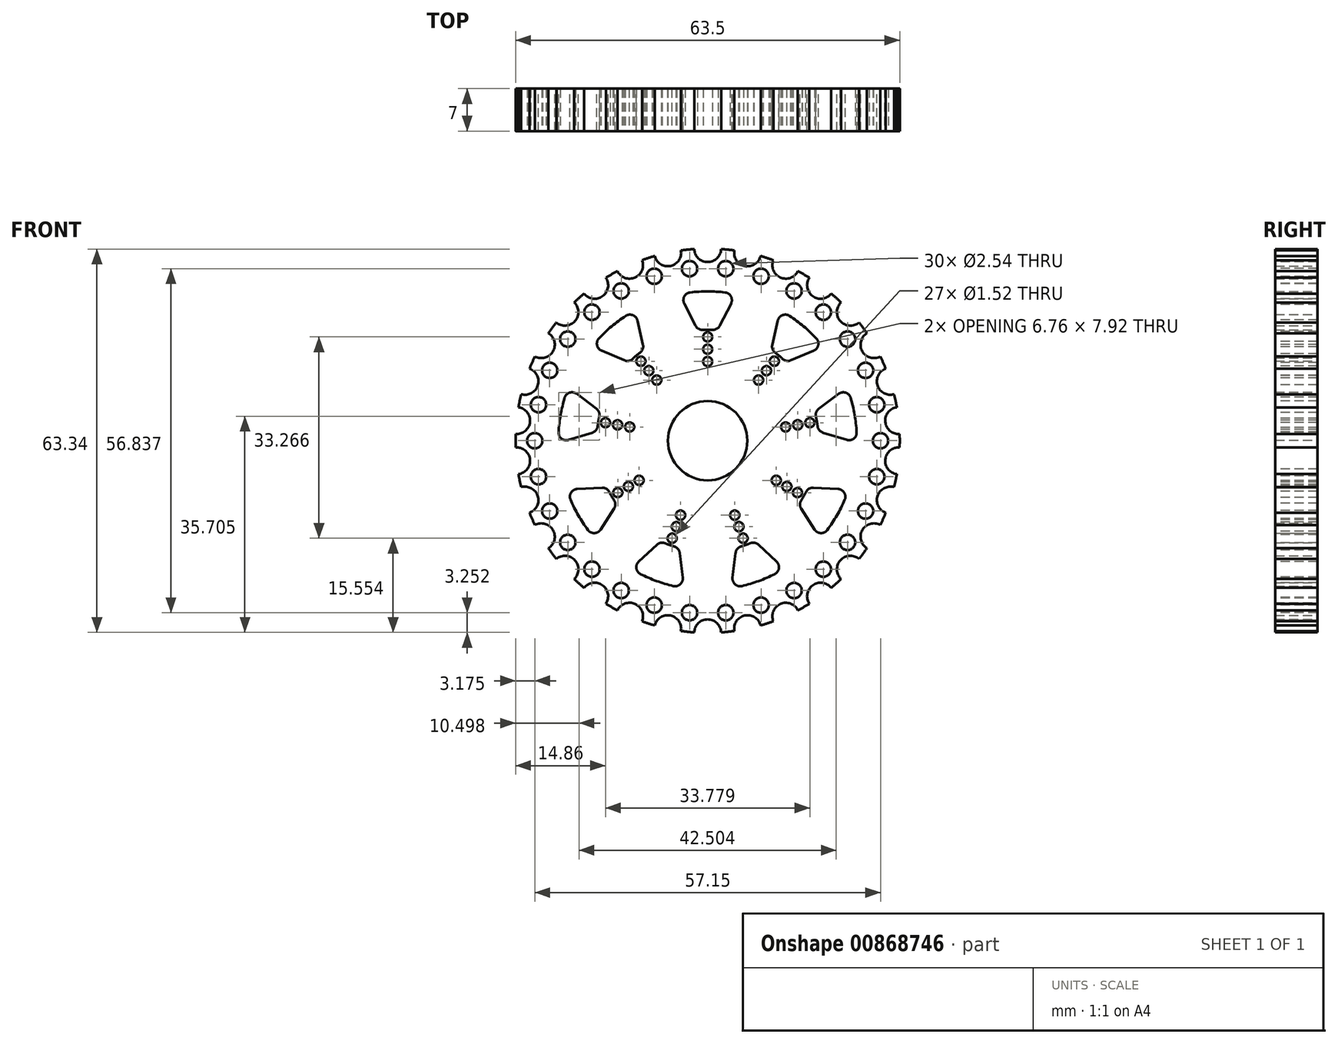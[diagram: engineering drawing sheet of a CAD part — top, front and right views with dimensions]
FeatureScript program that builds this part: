
annotation { "Feature Type Name" : "Feature", "Feature Type Description" : "" }
export const myFeature = defineFeature(function(context is Context, id is Id, definition is map)
    precondition{}
    {
        {
            var Q0;
            Q0=qCreatedBy(makeId("Front.planeOp"),FACE);
            var sketch = newSketch(context, id + "F0", { "sketchPlane" : qUnion([Q0])});
            skArc(sketch, "E0", {"start": v(-31.73, 1.1) * mm, "mid": v(-31.75, 0) * mm, "end": v(-31.73, -1.1) * mm});
            skPoint(sketch, "E1.end.orphan", {"position": v(-54.25, -98.6) * mm});
            skPoint(sketch, "E2.end.orphan", {"position": v(183.76, 0) * mm});
            skPoint(sketch, "E3.center.orphan", {"position": v(0, 98.6) * mm});
            skPoint(sketch, "E3.end.orphan", {"position": v(54.25, 98.6) * mm});
            skPoint(sketch, "E3.start.orphan", {"position": v(-54.25, 98.6) * mm});
            skCircle(sketch, "E4", {"center": v(0, 31.75) * mm, "radius": 2.22 * mm});
            skArc(sketch, "E5.9.0", {"start": v(-0.82, 33.81) * mm, "mid": v(-1.28, 29.93) * mm, "end": v(2.22, 31.67) * mm});
            skArc(sketch, "E5.10.0", {"start": v(-1.25, 33.59) * mm, "mid": v(-1.08, 29.8) * mm, "end": v(2.22, 31.67) * mm});
            skArc(sketch, "E5.13.0", {"start": v(-2.1, 32.46) * mm, "mid": v(-0.4, 29.56) * mm, "end": v(2.22, 31.67) * mm});
            skArc(sketch, "E5.18.0", {"start": v(-0.82, 33.81) * mm, "mid": v(-1.28, 29.93) * mm, "end": v(2.22, 31.67) * mm});
            skArc(sketch, "E5.19.0", {"start": v(-0.82, 33.81) * mm, "mid": v(-1.28, 29.93) * mm, "end": v(2.22, 31.67) * mm});
            skLineSegment(sketch, "E5.anchor1", {"start": v(0, 0) * mm, "end": v(0, 31.75) * mm, "construction": true});
            skLineSegment(sketch, "E5.anchor2", {"start": v(0, 0) * mm, "end": v(0, 31.75) * mm, "construction": true});
            skPoint(sketch, "E6.center", {"position": v(-2.61, -0.33) * mm});
            skArc(sketch, "E7.1.0", {"start": v(-8.76, 30.52) * mm, "mid": v(-6.14, 28.88) * mm, "end": v(-4.41, 31.44) * mm});
            skArc(sketch, "E7.2.0", {"start": v(-14.91, 28.03) * mm, "mid": v(-12, 26.97) * mm, "end": v(-10.85, 29.84) * mm});
            skArc(sketch, "E7.3.0", {"start": v(-20.41, 24.32) * mm, "mid": v(-17.36, 23.89) * mm, "end": v(-16.82, 26.93) * mm});
            skArc(sketch, "E7.4.0", {"start": v(-25.02, 19.54) * mm, "mid": v(-21.94, 19.76) * mm, "end": v(-22.05, 22.84) * mm});
            skArc(sketch, "E7.5.0", {"start": v(-28.54, 13.91) * mm, "mid": v(-25.57, 14.76) * mm, "end": v(-26.32, 17.76) * mm});
            skArc(sketch, "E7.6.0", {"start": v(-30.8, 7.67) * mm, "mid": v(-28.08, 9.12) * mm, "end": v(-29.44, 11.9) * mm});
            skArc(sketch, "E7.7.0", {"start": v(-31.73, 1.1) * mm, "mid": v(-29.37, 3.09) * mm, "end": v(-31.27, 5.52) * mm});
            skArc(sketch, "E7.8.0", {"start": v(-31.27, -5.52) * mm, "mid": v(-29.37, -3.09) * mm, "end": v(-31.73, -1.1) * mm});
            skArc(sketch, "E7.9.0", {"start": v(-29.44, -11.9) * mm, "mid": v(-28.08, -9.12) * mm, "end": v(-30.8, -7.67) * mm});
            skArc(sketch, "E7.10.0", {"start": v(-26.32, -17.76) * mm, "mid": v(-25.57, -14.76) * mm, "end": v(-28.54, -13.91) * mm});
            skArc(sketch, "E7.11.0", {"start": v(-22.05, -22.84) * mm, "mid": v(-21.94, -19.76) * mm, "end": v(-25.02, -19.54) * mm});
            skArc(sketch, "E7.12.0", {"start": v(-16.82, -26.93) * mm, "mid": v(-17.36, -23.89) * mm, "end": v(-20.41, -24.32) * mm});
            skArc(sketch, "E7.13.0", {"start": v(-10.85, -29.84) * mm, "mid": v(-12, -26.97) * mm, "end": v(-14.91, -28.03) * mm});
            skArc(sketch, "E7.14.0", {"start": v(-4.41, -31.44) * mm, "mid": v(-6.14, -28.88) * mm, "end": v(-8.76, -30.52) * mm});
            skArc(sketch, "E7.15.0", {"start": v(2.22, -31.67) * mm, "mid": v(0, -29.53) * mm, "end": v(-2.22, -31.67) * mm});
            skArc(sketch, "E7.16.0", {"start": v(8.76, -30.52) * mm, "mid": v(6.14, -28.88) * mm, "end": v(4.41, -31.44) * mm});
            skArc(sketch, "E7.17.0", {"start": v(14.91, -28.03) * mm, "mid": v(12, -26.97) * mm, "end": v(10.85, -29.84) * mm});
            skArc(sketch, "E7.18.0", {"start": v(20.41, -24.32) * mm, "mid": v(17.36, -23.89) * mm, "end": v(16.82, -26.93) * mm});
            skArc(sketch, "E7.19.0", {"start": v(25.02, -19.54) * mm, "mid": v(21.94, -19.76) * mm, "end": v(22.05, -22.84) * mm});
            skArc(sketch, "E7.20.0", {"start": v(28.54, -13.91) * mm, "mid": v(25.57, -14.76) * mm, "end": v(26.32, -17.76) * mm});
            skArc(sketch, "E7.21.0", {"start": v(30.8, -7.67) * mm, "mid": v(28.08, -9.12) * mm, "end": v(29.44, -11.9) * mm});
            skArc(sketch, "E7.22.0", {"start": v(31.73, -1.1) * mm, "mid": v(29.37, -3.09) * mm, "end": v(31.27, -5.52) * mm});
            skArc(sketch, "E7.23.0", {"start": v(31.27, 5.52) * mm, "mid": v(29.37, 3.09) * mm, "end": v(31.73, 1.1) * mm});
            skArc(sketch, "E7.24.0", {"start": v(29.44, 11.9) * mm, "mid": v(28.08, 9.12) * mm, "end": v(30.8, 7.67) * mm});
            skArc(sketch, "E7.25.0", {"start": v(26.32, 17.76) * mm, "mid": v(25.57, 14.76) * mm, "end": v(28.54, 13.91) * mm});
            skArc(sketch, "E7.26.0", {"start": v(22.05, 22.84) * mm, "mid": v(21.94, 19.76) * mm, "end": v(25.02, 19.54) * mm});
            skArc(sketch, "E7.27.0", {"start": v(16.82, 26.93) * mm, "mid": v(17.36, 23.89) * mm, "end": v(20.41, 24.32) * mm});
            skArc(sketch, "E7.28.0", {"start": v(10.85, 29.84) * mm, "mid": v(12, 26.97) * mm, "end": v(14.91, 28.03) * mm});
            skArc(sketch, "E7.29.0", {"start": v(4.41, 31.44) * mm, "mid": v(6.14, 28.88) * mm, "end": v(8.76, 30.52) * mm});
            skArc(sketch, "E8.trimOffspring", {"start": v(-30.8, 7.67) * mm, "mid": v(-31.06, 6.6) * mm, "end": v(-31.27, 5.52) * mm});
            skArc(sketch, "E9.trimOffspring", {"start": v(-28.54, 13.91) * mm, "mid": v(-29, 12.91) * mm, "end": v(-29.44, 11.9) * mm});
            skArc(sketch, "E10.trimOffspring", {"start": v(-25.02, 19.54) * mm, "mid": v(-25.69, 18.66) * mm, "end": v(-26.32, 17.76) * mm});
            skArc(sketch, "E11.trimOffspring", {"start": v(-20.41, 24.32) * mm, "mid": v(-21.24, 23.6) * mm, "end": v(-22.05, 22.84) * mm});
            skArc(sketch, "E12.trimOffspring", {"start": v(-14.91, 28.03) * mm, "mid": v(-15.88, 27.5) * mm, "end": v(-16.82, 26.93) * mm});
            skArc(sketch, "E13.trimOffspring", {"start": v(-8.76, 30.52) * mm, "mid": v(-9.81, 30.2) * mm, "end": v(-10.85, 29.84) * mm});
            skArc(sketch, "E14.trimOffspring", {"start": v(-2.22, 31.67) * mm, "mid": v(-3.32, 31.58) * mm, "end": v(-4.41, 31.44) * mm});
            skArc(sketch, "E15.trimOffspring", {"start": v(4.41, 31.44) * mm, "mid": v(3.32, 31.58) * mm, "end": v(2.22, 31.67) * mm});
            skArc(sketch, "E16.trimOffspring", {"start": v(10.85, 29.84) * mm, "mid": v(9.81, 30.2) * mm, "end": v(8.76, 30.52) * mm});
            skArc(sketch, "E17.trimOffspring", {"start": v(16.82, 26.93) * mm, "mid": v(15.88, 27.5) * mm, "end": v(14.91, 28.03) * mm});
            skArc(sketch, "E18.trimOffspring", {"start": v(22.05, 22.84) * mm, "mid": v(21.24, 23.6) * mm, "end": v(20.41, 24.32) * mm});
            skArc(sketch, "E19.trimOffspring", {"start": v(26.32, 17.76) * mm, "mid": v(25.69, 18.66) * mm, "end": v(25.02, 19.54) * mm});
            skArc(sketch, "E20.trimOffspring", {"start": v(29.44, 11.9) * mm, "mid": v(29, 12.91) * mm, "end": v(28.54, 13.91) * mm});
            skArc(sketch, "E21.trimOffspring", {"start": v(31.27, 5.52) * mm, "mid": v(31.06, 6.6) * mm, "end": v(30.8, 7.67) * mm});
            skArc(sketch, "E22.trimOffspring", {"start": v(31.73, -1.1) * mm, "mid": v(31.75, 0) * mm, "end": v(31.73, 1.1) * mm});
            skArc(sketch, "E23.trimOffspring", {"start": v(30.8, -7.67) * mm, "mid": v(31.06, -6.6) * mm, "end": v(31.27, -5.52) * mm});
            skArc(sketch, "E24.trimOffspring", {"start": v(28.54, -13.91) * mm, "mid": v(29, -12.91) * mm, "end": v(29.44, -11.9) * mm});
            skArc(sketch, "E25.trimOffspring", {"start": v(25.02, -19.54) * mm, "mid": v(25.69, -18.66) * mm, "end": v(26.32, -17.76) * mm});
            skArc(sketch, "E26.trimOffspring", {"start": v(20.41, -24.32) * mm, "mid": v(21.24, -23.6) * mm, "end": v(22.05, -22.84) * mm});
            skArc(sketch, "E27.trimOffspring", {"start": v(14.91, -28.03) * mm, "mid": v(15.87, -27.5) * mm, "end": v(16.82, -26.93) * mm});
            skArc(sketch, "E28.trimOffspring", {"start": v(-31.27, -5.52) * mm, "mid": v(-31.06, -6.6) * mm, "end": v(-30.8, -7.67) * mm});
            skArc(sketch, "E29.trimOffspring", {"start": v(-29.44, -11.9) * mm, "mid": v(-29, -12.91) * mm, "end": v(-28.54, -13.91) * mm});
            skArc(sketch, "E30.trimOffspring", {"start": v(-26.32, -17.76) * mm, "mid": v(-25.69, -18.66) * mm, "end": v(-25.02, -19.54) * mm});
            skArc(sketch, "E31.trimOffspring", {"start": v(-22.05, -22.84) * mm, "mid": v(-21.24, -23.6) * mm, "end": v(-20.41, -24.32) * mm});
            skArc(sketch, "E32.trimOffspring", {"start": v(-16.82, -26.93) * mm, "mid": v(-15.87, -27.5) * mm, "end": v(-14.91, -28.03) * mm});
            skArc(sketch, "E33.trimOffspring", {"start": v(-10.85, -29.84) * mm, "mid": v(-9.81, -30.2) * mm, "end": v(-8.76, -30.52) * mm});
            skArc(sketch, "E34.trimOffspring", {"start": v(-4.41, -31.44) * mm, "mid": v(-3.32, -31.58) * mm, "end": v(-2.22, -31.67) * mm});
            skArc(sketch, "E35.trimOffspring", {"start": v(2.22, -31.67) * mm, "mid": v(3.32, -31.58) * mm, "end": v(4.41, -31.44) * mm});
            skArc(sketch, "E36.trimOffspring", {"start": v(8.76, -30.52) * mm, "mid": v(9.81, -30.2) * mm, "end": v(10.85, -29.84) * mm});
            skCircle(sketch, "E37", {"center": v(0, 0) * mm, "radius": 6.35 * mm, "construction": true});
            skLineSegment(sketch, "E38", {"start": v(-3.87, 22.66) * mm, "end": v(-2, 19.01) * mm});
            skArc(sketch, "E39", {"start": v(-0.82, 18.32) * mm, "mid": v(-0.4, 18.33) * mm, "end": v(0, 18.34) * mm});
            skArc(sketch, "E40", {"start": v(-2.89, 24.5) * mm, "mid": v(-1.45, 24.63) * mm, "end": v(0, 24.67) * mm});
            skPoint(sketch, "E41.visualSharp", {"position": v(-4.67, 24.23) * mm});
            skArc(sketch, "E41.filletArc", {"start": v(-2.89, 24.5) * mm, "mid": v(-3.86, 23.84) * mm, "end": v(-3.87, 22.66) * mm});
            skPoint(sketch, "E42.visualSharp", {"position": v(-1.62, 18.27) * mm});
            skArc(sketch, "E42.filletArc", {"start": v(-2, 19.01) * mm, "mid": v(-1.51, 18.5) * mm, "end": v(-0.82, 18.32) * mm});
            skPoint(sketch, "E43.start.orphan", {"position": v(4.67, 24.23) * mm});
            skPoint(sketch, "E44.orphan", {"position": v(1.62, 18.27) * mm});
            skArc(sketch, "E45.MirrorCS", {"start": v(2.89, 24.5) * mm, "mid": v(1.45, 24.63) * mm, "end": v(0, 24.67) * mm});
            skArc(sketch, "E46.MirrorCS", {"start": v(2.89, 24.5) * mm, "mid": v(3.86, 23.84) * mm, "end": v(3.87, 22.66) * mm});
            skLineSegment(sketch, "E47.MirrorCS", {"start": v(3.87, 22.66) * mm, "end": v(2, 19.01) * mm});
            skArc(sketch, "E48.MirrorCS", {"start": v(2, 19.01) * mm, "mid": v(1.51, 18.5) * mm, "end": v(0.82, 18.32) * mm});
            skArc(sketch, "E49.MirrorCS", {"start": v(0.82, 18.32) * mm, "mid": v(0.4, 18.33) * mm, "end": v(0, 18.34) * mm});
            skLineSegment(sketch, "E50.anchor1", {"start": v(0, 0) * mm, "end": v(-1.62, 18.27) * mm, "construction": true});
            skLineSegment(sketch, "E50.anchor2", {"start": v(0, 0) * mm, "end": v(-1.62, 18.27) * mm, "construction": true});
            skPoint(sketch, "E51.1.0", {"position": v(-12, 21.56) * mm});
            skPoint(sketch, "E51.1.1", {"position": v(-19.15, 15.56) * mm});
            skLineSegment(sketch, "E51.1.2", {"start": v(-17.53, 14.88) * mm, "end": v(-13.75, 13.28) * mm});
            skLineSegment(sketch, "E51.1.3", {"start": v(-11.6, 19.85) * mm, "end": v(-10.69, 15.85) * mm});
            skArc(sketch, "E51.1.4", {"start": v(-13.54, 20.63) * mm, "mid": v(-14.73, 19.8) * mm, "end": v(-15.86, 18.9) * mm});
            skArc(sketch, "E51.1.5", {"start": v(-13.54, 20.63) * mm, "mid": v(-12.37, 20.74) * mm, "end": v(-11.6, 19.85) * mm});
            skArc(sketch, "E51.1.6", {"start": v(-17.96, 16.92) * mm, "mid": v(-16.94, 17.94) * mm, "end": v(-15.86, 18.9) * mm});
            skArc(sketch, "E51.1.7", {"start": v(-17.96, 16.92) * mm, "mid": v(-18.28, 15.78) * mm, "end": v(-17.53, 14.88) * mm});
            skLineSegment(sketch, "E51.1.8", {"start": v(-17.53, 14.88) * mm, "end": v(-13.75, 13.28) * mm});
            skArc(sketch, "E51.1.9", {"start": v(-13.54, 20.63) * mm, "mid": v(-14.73, 19.8) * mm, "end": v(-15.86, 18.9) * mm});
            skArc(sketch, "E51.1.10", {"start": v(-17.96, 16.92) * mm, "mid": v(-18.28, 15.78) * mm, "end": v(-17.53, 14.88) * mm});
            skPoint(sketch, "E51.1.11", {"position": v(-12, 21.56) * mm});
            skLineSegment(sketch, "E51.1.12", {"start": v(-11.6, 19.85) * mm, "end": v(-10.69, 15.85) * mm});
            skArc(sketch, "E51.1.13", {"start": v(-17.96, 16.92) * mm, "mid": v(-16.94, 17.94) * mm, "end": v(-15.86, 18.9) * mm});
            skPoint(sketch, "E51.1.14", {"position": v(-19.15, 15.56) * mm});
            skPoint(sketch, "E51.1.15", {"position": v(-10.5, 15.04) * mm});
            skPoint(sketch, "E51.1.16", {"position": v(-12.98, 12.95) * mm});
            skArc(sketch, "E51.1.17", {"start": v(-13.54, 20.63) * mm, "mid": v(-12.37, 20.74) * mm, "end": v(-11.6, 19.85) * mm});
            skArc(sketch, "E51.1.18", {"start": v(-17.96, 16.92) * mm, "mid": v(-18.28, 15.78) * mm, "end": v(-17.53, 14.88) * mm});
            skLineSegment(sketch, "E51.1.19", {"start": v(-17.53, 14.88) * mm, "end": v(-13.75, 13.28) * mm});
            skPoint(sketch, "E51.1.20", {"position": v(-12, 21.56) * mm});
            skArc(sketch, "E51.1.21", {"start": v(-13.54, 20.63) * mm, "mid": v(-14.73, 19.8) * mm, "end": v(-15.86, 18.9) * mm});
            skPoint(sketch, "E51.1.22", {"position": v(-10.5, 15.04) * mm});
            skArc(sketch, "E51.1.23", {"start": v(-17.96, 16.92) * mm, "mid": v(-16.94, 17.94) * mm, "end": v(-15.86, 18.9) * mm});
            skPoint(sketch, "E51.1.24", {"position": v(-12.98, 12.95) * mm});
            skPoint(sketch, "E51.1.25", {"position": v(-19.15, 15.56) * mm});
            skLineSegment(sketch, "E51.1.26", {"start": v(-11.6, 19.85) * mm, "end": v(-10.69, 15.85) * mm});
            skArc(sketch, "E51.1.27", {"start": v(-13.54, 20.63) * mm, "mid": v(-12.37, 20.74) * mm, "end": v(-11.6, 19.85) * mm});
            skLineSegment(sketch, "E51.1.28", {"start": v(-17.53, 14.88) * mm, "end": v(-13.75, 13.28) * mm});
            skPoint(sketch, "E51.1.29", {"position": v(-12.98, 12.95) * mm});
            skArc(sketch, "E51.1.30", {"start": v(-17.96, 16.92) * mm, "mid": v(-16.94, 17.94) * mm, "end": v(-15.86, 18.9) * mm});
            skPoint(sketch, "E51.1.31", {"position": v(-19.15, 15.56) * mm});
            skPoint(sketch, "E51.1.32", {"position": v(-12, 21.56) * mm});
            skLineSegment(sketch, "E51.1.33", {"start": v(-11.6, 19.85) * mm, "end": v(-10.69, 15.85) * mm});
            skArc(sketch, "E51.1.34", {"start": v(-13.54, 20.63) * mm, "mid": v(-14.73, 19.8) * mm, "end": v(-15.86, 18.9) * mm});
            skArc(sketch, "E51.1.35", {"start": v(-17.96, 16.92) * mm, "mid": v(-18.28, 15.78) * mm, "end": v(-17.53, 14.88) * mm});
            skArc(sketch, "E51.1.36", {"start": v(-13.54, 20.63) * mm, "mid": v(-12.37, 20.74) * mm, "end": v(-11.6, 19.85) * mm});
            skPoint(sketch, "E51.1.37", {"position": v(-10.5, 15.04) * mm});
            skArc(sketch, "E51.1.38", {"start": v(-13.54, 20.63) * mm, "mid": v(-14.73, 19.8) * mm, "end": v(-15.86, 18.9) * mm});
            skArc(sketch, "E51.1.39", {"start": v(-17.96, 16.92) * mm, "mid": v(-16.94, 17.94) * mm, "end": v(-15.86, 18.9) * mm});
            skLineSegment(sketch, "E51.1.40", {"start": v(-11.6, 19.85) * mm, "end": v(-10.69, 15.85) * mm});
            skPoint(sketch, "E51.1.41", {"position": v(-12, 21.56) * mm});
            skArc(sketch, "E51.1.42", {"start": v(-17.96, 16.92) * mm, "mid": v(-18.28, 15.78) * mm, "end": v(-17.53, 14.88) * mm});
            skPoint(sketch, "E51.1.43", {"position": v(-10.5, 15.04) * mm});
            skPoint(sketch, "E51.1.44", {"position": v(-19.15, 15.56) * mm});
            skPoint(sketch, "E51.1.45", {"position": v(-12.98, 12.95) * mm});
            skLineSegment(sketch, "E51.1.46", {"start": v(-17.53, 14.88) * mm, "end": v(-13.75, 13.28) * mm});
            skArc(sketch, "E51.1.47", {"start": v(-13.54, 20.63) * mm, "mid": v(-12.37, 20.74) * mm, "end": v(-11.6, 19.85) * mm});
            skPoint(sketch, "E51.1.48", {"position": v(-10.5, 15.04) * mm});
            skPoint(sketch, "E51.1.49", {"position": v(-12.98, 12.95) * mm});
            skArc(sketch, "E51.1.50", {"start": v(-10.69, 15.85) * mm, "mid": v(-10.73, 15.14) * mm, "end": v(-11.15, 14.56) * mm});
            skArc(sketch, "E51.1.51", {"start": v(-10.69, 15.85) * mm, "mid": v(-10.73, 15.14) * mm, "end": v(-11.15, 14.56) * mm});
            skArc(sketch, "E51.1.52", {"start": v(-13.75, 13.28) * mm, "mid": v(-13.04, 13.2) * mm, "end": v(-12.4, 13.5) * mm});
            skArc(sketch, "E51.1.53", {"start": v(-10.69, 15.85) * mm, "mid": v(-10.73, 15.14) * mm, "end": v(-11.15, 14.56) * mm});
            skArc(sketch, "E51.1.54", {"start": v(-10.69, 15.85) * mm, "mid": v(-10.73, 15.14) * mm, "end": v(-11.15, 14.56) * mm});
            skArc(sketch, "E51.1.55", {"start": v(-13.75, 13.28) * mm, "mid": v(-13.04, 13.2) * mm, "end": v(-12.4, 13.5) * mm});
            skArc(sketch, "E51.1.56", {"start": v(-10.69, 15.85) * mm, "mid": v(-10.73, 15.14) * mm, "end": v(-11.15, 14.56) * mm});
            skArc(sketch, "E51.1.57", {"start": v(-13.75, 13.28) * mm, "mid": v(-13.04, 13.2) * mm, "end": v(-12.4, 13.5) * mm});
            skArc(sketch, "E51.1.58", {"start": v(-11.15, 14.56) * mm, "mid": v(-11.47, 14.3) * mm, "end": v(-11.79, 14.05) * mm});
            skArc(sketch, "E51.1.59", {"start": v(-13.75, 13.28) * mm, "mid": v(-13.04, 13.2) * mm, "end": v(-12.4, 13.5) * mm});
            skArc(sketch, "E51.1.60", {"start": v(-12.4, 13.5) * mm, "mid": v(-12.1, 13.78) * mm, "end": v(-11.79, 14.05) * mm});
            skArc(sketch, "E51.1.61", {"start": v(-12.4, 13.5) * mm, "mid": v(-12.1, 13.78) * mm, "end": v(-11.79, 14.05) * mm});
            skArc(sketch, "E51.1.62", {"start": v(-13.75, 13.28) * mm, "mid": v(-13.04, 13.2) * mm, "end": v(-12.4, 13.5) * mm});
            skArc(sketch, "E51.1.63", {"start": v(-11.15, 14.56) * mm, "mid": v(-11.47, 14.3) * mm, "end": v(-11.79, 14.05) * mm});
            skArc(sketch, "E51.1.64", {"start": v(-12.4, 13.5) * mm, "mid": v(-12.1, 13.78) * mm, "end": v(-11.79, 14.05) * mm});
            skArc(sketch, "E51.1.65", {"start": v(-11.15, 14.56) * mm, "mid": v(-11.47, 14.3) * mm, "end": v(-11.79, 14.05) * mm});
            skArc(sketch, "E51.1.66", {"start": v(-11.15, 14.56) * mm, "mid": v(-11.47, 14.3) * mm, "end": v(-11.79, 14.05) * mm});
            skArc(sketch, "E51.1.67", {"start": v(-12.4, 13.5) * mm, "mid": v(-12.1, 13.78) * mm, "end": v(-11.79, 14.05) * mm});
            skArc(sketch, "E51.1.68", {"start": v(-12.4, 13.5) * mm, "mid": v(-12.1, 13.78) * mm, "end": v(-11.79, 14.05) * mm});
            skArc(sketch, "E51.1.69", {"start": v(-11.15, 14.56) * mm, "mid": v(-11.47, 14.3) * mm, "end": v(-11.79, 14.05) * mm});
            skPoint(sketch, "E51.2.0", {"position": v(-23.05, 8.8) * mm});
            skPoint(sketch, "E51.2.1", {"position": v(-24.67, -0.39) * mm});
            skLineSegment(sketch, "E51.2.2", {"start": v(-23, 0.13) * mm, "end": v(-19.07, 1.33) * mm});
            skLineSegment(sketch, "E51.2.3", {"start": v(-21.65, 7.74) * mm, "end": v(-18.37, 5.27) * mm});
            skArc(sketch, "E51.2.4", {"start": v(-23.63, 7.1) * mm, "mid": v(-24, 5.7) * mm, "end": v(-24.3, 4.28) * mm});
            skArc(sketch, "E51.2.5", {"start": v(-23.63, 7.1) * mm, "mid": v(-22.8, 7.94) * mm, "end": v(-21.65, 7.74) * mm});
            skArc(sketch, "E51.2.6", {"start": v(-24.63, 1.41) * mm, "mid": v(-24.5, 2.85) * mm, "end": v(-24.3, 4.28) * mm});
            skArc(sketch, "E51.2.7", {"start": v(-24.63, 1.41) * mm, "mid": v(-24.15, 0.34) * mm, "end": v(-23, 0.13) * mm});
            skLineSegment(sketch, "E51.2.8", {"start": v(-23, 0.13) * mm, "end": v(-19.07, 1.33) * mm});
            skArc(sketch, "E51.2.9", {"start": v(-23.63, 7.1) * mm, "mid": v(-24, 5.7) * mm, "end": v(-24.3, 4.28) * mm});
            skArc(sketch, "E51.2.10", {"start": v(-24.63, 1.41) * mm, "mid": v(-24.15, 0.34) * mm, "end": v(-23, 0.13) * mm});
            skPoint(sketch, "E51.2.11", {"position": v(-23.05, 8.8) * mm});
            skLineSegment(sketch, "E51.2.12", {"start": v(-21.65, 7.74) * mm, "end": v(-18.37, 5.27) * mm});
            skArc(sketch, "E51.2.13", {"start": v(-24.63, 1.41) * mm, "mid": v(-24.5, 2.85) * mm, "end": v(-24.3, 4.28) * mm});
            skPoint(sketch, "E51.2.14", {"position": v(-24.67, -0.39) * mm});
            skPoint(sketch, "E51.2.15", {"position": v(-17.7, 4.77) * mm});
            skPoint(sketch, "E51.2.16", {"position": v(-18.27, 1.57) * mm});
            skArc(sketch, "E51.2.17", {"start": v(-23.63, 7.1) * mm, "mid": v(-22.8, 7.94) * mm, "end": v(-21.65, 7.74) * mm});
            skArc(sketch, "E51.2.18", {"start": v(-24.63, 1.41) * mm, "mid": v(-24.15, 0.34) * mm, "end": v(-23, 0.13) * mm});
            skLineSegment(sketch, "E51.2.19", {"start": v(-23, 0.13) * mm, "end": v(-19.07, 1.33) * mm});
            skPoint(sketch, "E51.2.20", {"position": v(-23.05, 8.8) * mm});
            skArc(sketch, "E51.2.21", {"start": v(-23.63, 7.1) * mm, "mid": v(-24, 5.7) * mm, "end": v(-24.3, 4.28) * mm});
            skPoint(sketch, "E51.2.22", {"position": v(-17.7, 4.77) * mm});
            skArc(sketch, "E51.2.23", {"start": v(-24.63, 1.41) * mm, "mid": v(-24.5, 2.85) * mm, "end": v(-24.3, 4.28) * mm});
            skPoint(sketch, "E51.2.24", {"position": v(-18.27, 1.57) * mm});
            skPoint(sketch, "E51.2.25", {"position": v(-24.67, -0.39) * mm});
            skLineSegment(sketch, "E51.2.26", {"start": v(-21.65, 7.74) * mm, "end": v(-18.37, 5.27) * mm});
            skArc(sketch, "E51.2.27", {"start": v(-23.63, 7.1) * mm, "mid": v(-22.8, 7.94) * mm, "end": v(-21.65, 7.74) * mm});
            skLineSegment(sketch, "E51.2.28", {"start": v(-23, 0.13) * mm, "end": v(-19.07, 1.33) * mm});
            skPoint(sketch, "E51.2.29", {"position": v(-18.27, 1.57) * mm});
            skArc(sketch, "E51.2.30", {"start": v(-24.63, 1.41) * mm, "mid": v(-24.5, 2.85) * mm, "end": v(-24.3, 4.28) * mm});
            skPoint(sketch, "E51.2.31", {"position": v(-24.67, -0.39) * mm});
            skPoint(sketch, "E51.2.32", {"position": v(-23.05, 8.8) * mm});
            skLineSegment(sketch, "E51.2.33", {"start": v(-21.65, 7.74) * mm, "end": v(-18.37, 5.27) * mm});
            skArc(sketch, "E51.2.34", {"start": v(-23.63, 7.1) * mm, "mid": v(-24, 5.7) * mm, "end": v(-24.3, 4.28) * mm});
            skArc(sketch, "E51.2.35", {"start": v(-24.63, 1.41) * mm, "mid": v(-24.15, 0.34) * mm, "end": v(-23, 0.13) * mm});
            skArc(sketch, "E51.2.36", {"start": v(-23.63, 7.1) * mm, "mid": v(-22.8, 7.94) * mm, "end": v(-21.65, 7.74) * mm});
            skPoint(sketch, "E51.2.37", {"position": v(-17.7, 4.77) * mm});
            skArc(sketch, "E51.2.38", {"start": v(-23.63, 7.1) * mm, "mid": v(-24, 5.7) * mm, "end": v(-24.3, 4.28) * mm});
            skArc(sketch, "E51.2.39", {"start": v(-24.63, 1.41) * mm, "mid": v(-24.5, 2.85) * mm, "end": v(-24.3, 4.28) * mm});
            skLineSegment(sketch, "E51.2.40", {"start": v(-21.65, 7.74) * mm, "end": v(-18.37, 5.27) * mm});
            skPoint(sketch, "E51.2.41", {"position": v(-23.05, 8.8) * mm});
            skArc(sketch, "E51.2.42", {"start": v(-24.63, 1.41) * mm, "mid": v(-24.15, 0.34) * mm, "end": v(-23, 0.13) * mm});
            skPoint(sketch, "E51.2.43", {"position": v(-17.7, 4.77) * mm});
            skPoint(sketch, "E51.2.44", {"position": v(-24.67, -0.39) * mm});
            skPoint(sketch, "E51.2.45", {"position": v(-18.27, 1.57) * mm});
            skLineSegment(sketch, "E51.2.46", {"start": v(-23, 0.13) * mm, "end": v(-19.07, 1.33) * mm});
            skArc(sketch, "E51.2.47", {"start": v(-23.63, 7.1) * mm, "mid": v(-22.8, 7.94) * mm, "end": v(-21.65, 7.74) * mm});
            skPoint(sketch, "E51.2.48", {"position": v(-17.7, 4.77) * mm});
            skPoint(sketch, "E51.2.49", {"position": v(-18.27, 1.57) * mm});
            skArc(sketch, "E51.2.50", {"start": v(-18.37, 5.27) * mm, "mid": v(-17.95, 4.7) * mm, "end": v(-17.9, 3.98) * mm});
            skArc(sketch, "E51.2.51", {"start": v(-18.37, 5.27) * mm, "mid": v(-17.95, 4.7) * mm, "end": v(-17.9, 3.98) * mm});
            skArc(sketch, "E51.2.52", {"start": v(-19.07, 1.33) * mm, "mid": v(-18.47, 1.72) * mm, "end": v(-18.18, 2.38) * mm});
            skArc(sketch, "E51.2.53", {"start": v(-18.37, 5.27) * mm, "mid": v(-17.95, 4.7) * mm, "end": v(-17.9, 3.98) * mm});
            skArc(sketch, "E51.2.54", {"start": v(-18.37, 5.27) * mm, "mid": v(-17.95, 4.7) * mm, "end": v(-17.9, 3.98) * mm});
            skArc(sketch, "E51.2.55", {"start": v(-19.07, 1.33) * mm, "mid": v(-18.47, 1.72) * mm, "end": v(-18.18, 2.38) * mm});
            skArc(sketch, "E51.2.56", {"start": v(-18.37, 5.27) * mm, "mid": v(-17.95, 4.7) * mm, "end": v(-17.9, 3.98) * mm});
            skArc(sketch, "E51.2.57", {"start": v(-19.07, 1.33) * mm, "mid": v(-18.47, 1.72) * mm, "end": v(-18.18, 2.38) * mm});
            skArc(sketch, "E51.2.58", {"start": v(-17.9, 3.98) * mm, "mid": v(-17.98, 3.59) * mm, "end": v(-18.06, 3.18) * mm});
            skArc(sketch, "E51.2.59", {"start": v(-19.07, 1.33) * mm, "mid": v(-18.47, 1.72) * mm, "end": v(-18.18, 2.38) * mm});
            skArc(sketch, "E51.2.60", {"start": v(-18.18, 2.38) * mm, "mid": v(-18.12, 2.78) * mm, "end": v(-18.06, 3.18) * mm});
            skArc(sketch, "E51.2.61", {"start": v(-18.18, 2.38) * mm, "mid": v(-18.12, 2.78) * mm, "end": v(-18.06, 3.18) * mm});
            skArc(sketch, "E51.2.62", {"start": v(-19.07, 1.33) * mm, "mid": v(-18.47, 1.72) * mm, "end": v(-18.18, 2.38) * mm});
            skArc(sketch, "E51.2.63", {"start": v(-17.9, 3.98) * mm, "mid": v(-17.98, 3.59) * mm, "end": v(-18.06, 3.18) * mm});
            skArc(sketch, "E51.2.64", {"start": v(-18.18, 2.38) * mm, "mid": v(-18.12, 2.78) * mm, "end": v(-18.06, 3.18) * mm});
            skArc(sketch, "E51.2.65", {"start": v(-17.9, 3.98) * mm, "mid": v(-17.98, 3.59) * mm, "end": v(-18.06, 3.18) * mm});
            skArc(sketch, "E51.2.66", {"start": v(-17.9, 3.98) * mm, "mid": v(-17.98, 3.59) * mm, "end": v(-18.06, 3.18) * mm});
            skArc(sketch, "E51.2.67", {"start": v(-18.18, 2.38) * mm, "mid": v(-18.12, 2.78) * mm, "end": v(-18.06, 3.18) * mm});
            skArc(sketch, "E51.2.68", {"start": v(-18.18, 2.38) * mm, "mid": v(-18.12, 2.78) * mm, "end": v(-18.06, 3.18) * mm});
            skArc(sketch, "E51.2.69", {"start": v(-17.9, 3.98) * mm, "mid": v(-17.98, 3.59) * mm, "end": v(-18.06, 3.18) * mm});
            skPoint(sketch, "E52.0.3.0", {"position": v(-15, -10.54) * mm});
            skPoint(sketch, "E52.1.3.0", {"position": v(-18.65, -16.15) * mm});
            skLineSegment(sketch, "E52.2.3.0", {"start": v(-17.7, -14.68) * mm, "end": v(-15.46, -11.24) * mm});
            skLineSegment(sketch, "E52.5.3.0", {"start": v(-21.56, -7.98) * mm, "end": v(-17.47, -7.77) * mm});
            skArc(sketch, "E52.8.3.0", {"start": v(-22.66, -9.75) * mm, "mid": v(-22.05, -11.06) * mm, "end": v(-21.37, -12.34) * mm});
            skArc(sketch, "E52.12.3.0", {"start": v(-22.66, -9.75) * mm, "mid": v(-22.58, -8.58) * mm, "end": v(-21.56, -7.98) * mm});
            skArc(sketch, "E52.16.3.0", {"start": v(-19.78, -14.75) * mm, "mid": v(-20.6, -13.57) * mm, "end": v(-21.37, -12.34) * mm});
            skArc(sketch, "E52.20.3.0", {"start": v(-19.78, -14.75) * mm, "mid": v(-18.72, -15.26) * mm, "end": v(-17.7, -14.68) * mm});
            skLineSegment(sketch, "E52.24.3.0", {"start": v(-17.7, -14.68) * mm, "end": v(-15.46, -11.24) * mm});
            skArc(sketch, "E52.27.3.0", {"start": v(-22.66, -9.75) * mm, "mid": v(-22.05, -11.06) * mm, "end": v(-21.37, -12.34) * mm});
            skArc(sketch, "E52.31.3.0", {"start": v(-19.78, -14.75) * mm, "mid": v(-18.72, -15.26) * mm, "end": v(-17.7, -14.68) * mm});
            skPoint(sketch, "E52.35.3.0", {"position": v(-23.31, -8.07) * mm});
            skLineSegment(sketch, "E52.36.3.0", {"start": v(-21.56, -7.98) * mm, "end": v(-17.47, -7.77) * mm});
            skArc(sketch, "E52.39.3.0", {"start": v(-19.78, -14.75) * mm, "mid": v(-20.6, -13.57) * mm, "end": v(-21.37, -12.34) * mm});
            skPoint(sketch, "E52.43.3.0", {"position": v(-18.65, -16.15) * mm});
            skPoint(sketch, "E52.44.3.0", {"position": v(-16.63, -7.73) * mm});
            skPoint(sketch, "E52.45.3.0", {"position": v(-23.31, -8.07) * mm});
            skArc(sketch, "E52.46.3.0", {"start": v(-22.66, -9.75) * mm, "mid": v(-22.58, -8.58) * mm, "end": v(-21.56, -7.98) * mm});
            skArc(sketch, "E52.50.3.0", {"start": v(-19.78, -14.75) * mm, "mid": v(-18.72, -15.26) * mm, "end": v(-17.7, -14.68) * mm});
            skLineSegment(sketch, "E52.54.3.0", {"start": v(-17.7, -14.68) * mm, "end": v(-15.46, -11.24) * mm});
            skPoint(sketch, "E52.57.3.0", {"position": v(-23.31, -8.07) * mm});
            skArc(sketch, "E52.58.3.0", {"start": v(-22.66, -9.75) * mm, "mid": v(-22.05, -11.06) * mm, "end": v(-21.37, -12.34) * mm});
            skPoint(sketch, "E52.62.3.0", {"position": v(-16.63, -7.73) * mm});
            skArc(sketch, "E52.63.3.0", {"start": v(-19.78, -14.75) * mm, "mid": v(-20.6, -13.57) * mm, "end": v(-21.37, -12.34) * mm});
            skPoint(sketch, "E52.67.3.0", {"position": v(-15, -10.54) * mm});
            skPoint(sketch, "E52.68.3.0", {"position": v(-18.65, -16.15) * mm});
            skLineSegment(sketch, "E52.69.3.0", {"start": v(-21.56, -7.98) * mm, "end": v(-17.47, -7.77) * mm});
            skArc(sketch, "E52.72.3.0", {"start": v(-22.66, -9.75) * mm, "mid": v(-22.58, -8.58) * mm, "end": v(-21.56, -7.98) * mm});
            skLineSegment(sketch, "E52.76.3.0", {"start": v(-17.7, -14.68) * mm, "end": v(-15.46, -11.24) * mm});
            skPoint(sketch, "E52.79.3.0", {"position": v(-15, -10.54) * mm});
            skArc(sketch, "E52.80.3.0", {"start": v(-19.78, -14.75) * mm, "mid": v(-20.6, -13.57) * mm, "end": v(-21.37, -12.34) * mm});
            skPoint(sketch, "E52.84.3.0", {"position": v(-18.65, -16.15) * mm});
            skPoint(sketch, "E52.85.3.0", {"position": v(-23.31, -8.07) * mm});
            skLineSegment(sketch, "E52.86.3.0", {"start": v(-21.56, -7.98) * mm, "end": v(-17.47, -7.77) * mm});
            skArc(sketch, "E52.89.3.0", {"start": v(-22.66, -9.75) * mm, "mid": v(-22.05, -11.06) * mm, "end": v(-21.37, -12.34) * mm});
            skArc(sketch, "E52.93.3.0", {"start": v(-19.78, -14.75) * mm, "mid": v(-18.72, -15.26) * mm, "end": v(-17.7, -14.68) * mm});
            skArc(sketch, "E52.97.3.0", {"start": v(-22.66, -9.75) * mm, "mid": v(-22.58, -8.58) * mm, "end": v(-21.56, -7.98) * mm});
            skPoint(sketch, "E52.101.3.0", {"position": v(-16.63, -7.73) * mm});
            skArc(sketch, "E52.102.3.0", {"start": v(-22.66, -9.75) * mm, "mid": v(-22.05, -11.06) * mm, "end": v(-21.37, -12.34) * mm});
            skArc(sketch, "E52.106.3.0", {"start": v(-19.78, -14.75) * mm, "mid": v(-20.6, -13.57) * mm, "end": v(-21.37, -12.34) * mm});
            skLineSegment(sketch, "E52.110.3.0", {"start": v(-21.56, -7.98) * mm, "end": v(-17.47, -7.77) * mm});
            skPoint(sketch, "E52.113.3.0", {"position": v(-23.31, -8.07) * mm});
            skArc(sketch, "E52.114.3.0", {"start": v(-19.78, -14.75) * mm, "mid": v(-18.72, -15.26) * mm, "end": v(-17.7, -14.68) * mm});
            skPoint(sketch, "E52.118.3.0", {"position": v(-16.63, -7.73) * mm});
            skPoint(sketch, "E52.119.3.0", {"position": v(-18.65, -16.15) * mm});
            skPoint(sketch, "E52.120.3.0", {"position": v(-15, -10.54) * mm});
            skLineSegment(sketch, "E52.121.3.0", {"start": v(-17.7, -14.68) * mm, "end": v(-15.46, -11.24) * mm});
            skArc(sketch, "E52.124.3.0", {"start": v(-22.66, -9.75) * mm, "mid": v(-22.58, -8.58) * mm, "end": v(-21.56, -7.98) * mm});
            skPoint(sketch, "E52.128.3.0", {"position": v(-16.63, -7.73) * mm});
            skPoint(sketch, "E52.129.3.0", {"position": v(-15, -10.54) * mm});
            skArc(sketch, "E52.130.3.0", {"start": v(-17.47, -7.77) * mm, "mid": v(-16.77, -7.94) * mm, "end": v(-16.27, -8.45) * mm});
            skArc(sketch, "E52.134.3.0", {"start": v(-17.47, -7.77) * mm, "mid": v(-16.77, -7.94) * mm, "end": v(-16.27, -8.45) * mm});
            skArc(sketch, "E52.138.3.0", {"start": v(-15.46, -11.24) * mm, "mid": v(-15.26, -10.55) * mm, "end": v(-15.46, -9.87) * mm});
            skArc(sketch, "E52.142.3.0", {"start": v(-17.47, -7.77) * mm, "mid": v(-16.77, -7.94) * mm, "end": v(-16.27, -8.45) * mm});
            skArc(sketch, "E52.146.3.0", {"start": v(-17.47, -7.77) * mm, "mid": v(-16.77, -7.94) * mm, "end": v(-16.27, -8.45) * mm});
            skArc(sketch, "E52.150.3.0", {"start": v(-15.46, -11.24) * mm, "mid": v(-15.26, -10.55) * mm, "end": v(-15.46, -9.87) * mm});
            skArc(sketch, "E52.154.3.0", {"start": v(-17.47, -7.77) * mm, "mid": v(-16.77, -7.94) * mm, "end": v(-16.27, -8.45) * mm});
            skArc(sketch, "E52.158.3.0", {"start": v(-15.46, -11.24) * mm, "mid": v(-15.26, -10.55) * mm, "end": v(-15.46, -9.87) * mm});
            skArc(sketch, "E52.162.3.0", {"start": v(-16.27, -8.45) * mm, "mid": v(-16.08, -8.81) * mm, "end": v(-15.88, -9.17) * mm});
            skArc(sketch, "E52.166.3.0", {"start": v(-15.46, -11.24) * mm, "mid": v(-15.26, -10.55) * mm, "end": v(-15.46, -9.87) * mm});
            skArc(sketch, "E52.170.3.0", {"start": v(-15.46, -9.87) * mm, "mid": v(-15.67, -9.52) * mm, "end": v(-15.88, -9.17) * mm});
            skArc(sketch, "E52.174.3.0", {"start": v(-15.46, -9.87) * mm, "mid": v(-15.67, -9.52) * mm, "end": v(-15.88, -9.17) * mm});
            skArc(sketch, "E52.178.3.0", {"start": v(-15.46, -11.24) * mm, "mid": v(-15.26, -10.55) * mm, "end": v(-15.46, -9.87) * mm});
            skArc(sketch, "E52.182.3.0", {"start": v(-16.27, -8.45) * mm, "mid": v(-16.08, -8.81) * mm, "end": v(-15.88, -9.17) * mm});
            skArc(sketch, "E52.186.3.0", {"start": v(-15.46, -9.87) * mm, "mid": v(-15.67, -9.52) * mm, "end": v(-15.88, -9.17) * mm});
            skArc(sketch, "E52.190.3.0", {"start": v(-16.27, -8.45) * mm, "mid": v(-16.08, -8.81) * mm, "end": v(-15.88, -9.17) * mm});
            skArc(sketch, "E52.194.3.0", {"start": v(-16.27, -8.45) * mm, "mid": v(-16.08, -8.81) * mm, "end": v(-15.88, -9.17) * mm});
            skArc(sketch, "E52.198.3.0", {"start": v(-15.46, -9.87) * mm, "mid": v(-15.67, -9.52) * mm, "end": v(-15.88, -9.17) * mm});
            skArc(sketch, "E52.202.3.0", {"start": v(-15.46, -9.87) * mm, "mid": v(-15.67, -9.52) * mm, "end": v(-15.88, -9.17) * mm});
            skArc(sketch, "E52.206.3.0", {"start": v(-16.27, -8.45) * mm, "mid": v(-16.08, -8.81) * mm, "end": v(-15.88, -9.17) * mm});
            skPoint(sketch, "E52.0.4.0", {"position": v(-4.72, -17.72) * mm});
            skPoint(sketch, "E52.1.4.0", {"position": v(-3.9, -24.36) * mm});
            skLineSegment(sketch, "E52.2.4.0", {"start": v(-4.12, -22.62) * mm, "end": v(-4.62, -18.55) * mm});
            skLineSegment(sketch, "E52.5.4.0", {"start": v(-11.39, -19.98) * mm, "end": v(-8.38, -17.18) * mm});
            skArc(sketch, "E52.8.4.0", {"start": v(-11.1, -22.04) * mm, "mid": v(-9.78, -22.65) * mm, "end": v(-8.44, -23.18) * mm});
            skArc(sketch, "E52.12.4.0", {"start": v(-11.1, -22.04) * mm, "mid": v(-11.78, -21.08) * mm, "end": v(-11.39, -19.98) * mm});
            skArc(sketch, "E52.16.4.0", {"start": v(-5.67, -24.01) * mm, "mid": v(-7.07, -23.64) * mm, "end": v(-8.44, -23.18) * mm});
            skArc(sketch, "E52.20.4.0", {"start": v(-5.67, -24.01) * mm, "mid": v(-4.53, -23.72) * mm, "end": v(-4.12, -22.62) * mm});
            skLineSegment(sketch, "E52.24.4.0", {"start": v(-4.12, -22.62) * mm, "end": v(-4.62, -18.55) * mm});
            skArc(sketch, "E52.27.4.0", {"start": v(-11.1, -22.04) * mm, "mid": v(-9.78, -22.65) * mm, "end": v(-8.44, -23.18) * mm});
            skArc(sketch, "E52.31.4.0", {"start": v(-5.67, -24.01) * mm, "mid": v(-4.53, -23.72) * mm, "end": v(-4.12, -22.62) * mm});
            skPoint(sketch, "E52.35.4.0", {"position": v(-12.67, -21.17) * mm});
            skLineSegment(sketch, "E52.36.4.0", {"start": v(-11.39, -19.98) * mm, "end": v(-8.38, -17.18) * mm});
            skArc(sketch, "E52.39.4.0", {"start": v(-5.67, -24.01) * mm, "mid": v(-7.07, -23.64) * mm, "end": v(-8.44, -23.18) * mm});
            skPoint(sketch, "E52.43.4.0", {"position": v(-3.9, -24.36) * mm});
            skPoint(sketch, "E52.44.4.0", {"position": v(-7.77, -16.6) * mm});
            skPoint(sketch, "E52.45.4.0", {"position": v(-12.67, -21.17) * mm});
            skArc(sketch, "E52.46.4.0", {"start": v(-11.1, -22.04) * mm, "mid": v(-11.78, -21.08) * mm, "end": v(-11.39, -19.98) * mm});
            skArc(sketch, "E52.50.4.0", {"start": v(-5.67, -24.01) * mm, "mid": v(-4.53, -23.72) * mm, "end": v(-4.12, -22.62) * mm});
            skLineSegment(sketch, "E52.54.4.0", {"start": v(-4.12, -22.62) * mm, "end": v(-4.62, -18.55) * mm});
            skPoint(sketch, "E52.57.4.0", {"position": v(-12.67, -21.17) * mm});
            skArc(sketch, "E52.58.4.0", {"start": v(-11.1, -22.04) * mm, "mid": v(-9.78, -22.65) * mm, "end": v(-8.44, -23.18) * mm});
            skPoint(sketch, "E52.62.4.0", {"position": v(-7.77, -16.6) * mm});
            skArc(sketch, "E52.63.4.0", {"start": v(-5.67, -24.01) * mm, "mid": v(-7.07, -23.64) * mm, "end": v(-8.44, -23.18) * mm});
            skPoint(sketch, "E52.67.4.0", {"position": v(-4.72, -17.72) * mm});
            skPoint(sketch, "E52.68.4.0", {"position": v(-3.9, -24.36) * mm});
            skLineSegment(sketch, "E52.69.4.0", {"start": v(-11.39, -19.98) * mm, "end": v(-8.38, -17.18) * mm});
            skArc(sketch, "E52.72.4.0", {"start": v(-11.1, -22.04) * mm, "mid": v(-11.78, -21.08) * mm, "end": v(-11.39, -19.98) * mm});
            skLineSegment(sketch, "E52.76.4.0", {"start": v(-4.12, -22.62) * mm, "end": v(-4.62, -18.55) * mm});
            skPoint(sketch, "E52.79.4.0", {"position": v(-4.72, -17.72) * mm});
            skArc(sketch, "E52.80.4.0", {"start": v(-5.67, -24.01) * mm, "mid": v(-7.07, -23.64) * mm, "end": v(-8.44, -23.18) * mm});
            skPoint(sketch, "E52.84.4.0", {"position": v(-3.9, -24.36) * mm});
            skPoint(sketch, "E52.85.4.0", {"position": v(-12.67, -21.17) * mm});
            skLineSegment(sketch, "E52.86.4.0", {"start": v(-11.39, -19.98) * mm, "end": v(-8.38, -17.18) * mm});
            skArc(sketch, "E52.89.4.0", {"start": v(-11.1, -22.04) * mm, "mid": v(-9.78, -22.65) * mm, "end": v(-8.44, -23.18) * mm});
            skArc(sketch, "E52.93.4.0", {"start": v(-5.67, -24.01) * mm, "mid": v(-4.53, -23.72) * mm, "end": v(-4.12, -22.62) * mm});
            skArc(sketch, "E52.97.4.0", {"start": v(-11.1, -22.04) * mm, "mid": v(-11.78, -21.08) * mm, "end": v(-11.39, -19.98) * mm});
            skPoint(sketch, "E52.101.4.0", {"position": v(-7.77, -16.6) * mm});
            skArc(sketch, "E52.102.4.0", {"start": v(-11.1, -22.04) * mm, "mid": v(-9.78, -22.65) * mm, "end": v(-8.44, -23.18) * mm});
            skArc(sketch, "E52.106.4.0", {"start": v(-5.67, -24.01) * mm, "mid": v(-7.07, -23.64) * mm, "end": v(-8.44, -23.18) * mm});
            skLineSegment(sketch, "E52.110.4.0", {"start": v(-11.39, -19.98) * mm, "end": v(-8.38, -17.18) * mm});
            skPoint(sketch, "E52.113.4.0", {"position": v(-12.67, -21.17) * mm});
            skArc(sketch, "E52.114.4.0", {"start": v(-5.67, -24.01) * mm, "mid": v(-4.53, -23.72) * mm, "end": v(-4.12, -22.62) * mm});
            skPoint(sketch, "E52.118.4.0", {"position": v(-7.77, -16.6) * mm});
            skPoint(sketch, "E52.119.4.0", {"position": v(-3.9, -24.36) * mm});
            skPoint(sketch, "E52.120.4.0", {"position": v(-4.72, -17.72) * mm});
            skLineSegment(sketch, "E52.121.4.0", {"start": v(-4.12, -22.62) * mm, "end": v(-4.62, -18.55) * mm});
            skArc(sketch, "E52.124.4.0", {"start": v(-11.1, -22.04) * mm, "mid": v(-11.78, -21.08) * mm, "end": v(-11.39, -19.98) * mm});
            skPoint(sketch, "E52.128.4.0", {"position": v(-7.77, -16.6) * mm});
            skPoint(sketch, "E52.129.4.0", {"position": v(-4.72, -17.72) * mm});
            skArc(sketch, "E52.130.4.0", {"start": v(-8.38, -17.18) * mm, "mid": v(-7.74, -16.86) * mm, "end": v(-7.03, -16.94) * mm});
            skArc(sketch, "E52.134.4.0", {"start": v(-8.38, -17.18) * mm, "mid": v(-7.74, -16.86) * mm, "end": v(-7.03, -16.94) * mm});
            skArc(sketch, "E52.138.4.0", {"start": v(-4.62, -18.55) * mm, "mid": v(-4.9, -17.9) * mm, "end": v(-5.5, -17.5) * mm});
            skArc(sketch, "E52.142.4.0", {"start": v(-8.38, -17.18) * mm, "mid": v(-7.74, -16.86) * mm, "end": v(-7.03, -16.94) * mm});
            skArc(sketch, "E52.146.4.0", {"start": v(-8.38, -17.18) * mm, "mid": v(-7.74, -16.86) * mm, "end": v(-7.03, -16.94) * mm});
            skArc(sketch, "E52.150.4.0", {"start": v(-4.62, -18.55) * mm, "mid": v(-4.9, -17.9) * mm, "end": v(-5.5, -17.5) * mm});
            skArc(sketch, "E52.154.4.0", {"start": v(-8.38, -17.18) * mm, "mid": v(-7.74, -16.86) * mm, "end": v(-7.03, -16.94) * mm});
            skArc(sketch, "E52.158.4.0", {"start": v(-4.62, -18.55) * mm, "mid": v(-4.9, -17.9) * mm, "end": v(-5.5, -17.5) * mm});
            skArc(sketch, "E52.162.4.0", {"start": v(-7.03, -16.94) * mm, "mid": v(-6.65, -17.09) * mm, "end": v(-6.27, -17.23) * mm});
            skArc(sketch, "E52.166.4.0", {"start": v(-4.62, -18.55) * mm, "mid": v(-4.9, -17.9) * mm, "end": v(-5.5, -17.5) * mm});
            skArc(sketch, "E52.170.4.0", {"start": v(-5.5, -17.5) * mm, "mid": v(-5.89, -17.37) * mm, "end": v(-6.27, -17.23) * mm});
            skArc(sketch, "E52.174.4.0", {"start": v(-5.5, -17.5) * mm, "mid": v(-5.89, -17.37) * mm, "end": v(-6.27, -17.23) * mm});
            skArc(sketch, "E52.178.4.0", {"start": v(-4.62, -18.55) * mm, "mid": v(-4.9, -17.9) * mm, "end": v(-5.5, -17.5) * mm});
            skArc(sketch, "E52.182.4.0", {"start": v(-7.03, -16.94) * mm, "mid": v(-6.65, -17.09) * mm, "end": v(-6.27, -17.23) * mm});
            skArc(sketch, "E52.186.4.0", {"start": v(-5.5, -17.5) * mm, "mid": v(-5.89, -17.37) * mm, "end": v(-6.27, -17.23) * mm});
            skArc(sketch, "E52.190.4.0", {"start": v(-7.03, -16.94) * mm, "mid": v(-6.65, -17.09) * mm, "end": v(-6.27, -17.23) * mm});
            skArc(sketch, "E52.194.4.0", {"start": v(-7.03, -16.94) * mm, "mid": v(-6.65, -17.09) * mm, "end": v(-6.27, -17.23) * mm});
            skArc(sketch, "E52.198.4.0", {"start": v(-5.5, -17.5) * mm, "mid": v(-5.89, -17.37) * mm, "end": v(-6.27, -17.23) * mm});
            skArc(sketch, "E52.202.4.0", {"start": v(-5.5, -17.5) * mm, "mid": v(-5.89, -17.37) * mm, "end": v(-6.27, -17.23) * mm});
            skArc(sketch, "E52.206.4.0", {"start": v(-7.03, -16.94) * mm, "mid": v(-6.65, -17.09) * mm, "end": v(-6.27, -17.23) * mm});
            skPoint(sketch, "E53.0.5.0", {"position": v(7.77, -16.6) * mm});
            skPoint(sketch, "E53.1.5.0", {"position": v(12.67, -21.17) * mm});
            skLineSegment(sketch, "E53.2.5.0", {"start": v(11.39, -19.98) * mm, "end": v(8.38, -17.18) * mm});
            skLineSegment(sketch, "E53.5.5.0", {"start": v(4.12, -22.62) * mm, "end": v(4.62, -18.55) * mm});
            skArc(sketch, "E53.8.5.0", {"start": v(5.67, -24.01) * mm, "mid": v(7.07, -23.64) * mm, "end": v(8.44, -23.18) * mm});
            skArc(sketch, "E53.12.5.0", {"start": v(5.67, -24.01) * mm, "mid": v(4.53, -23.72) * mm, "end": v(4.12, -22.62) * mm});
            skArc(sketch, "E53.16.5.0", {"start": v(11.1, -22.04) * mm, "mid": v(9.78, -22.65) * mm, "end": v(8.44, -23.18) * mm});
            skArc(sketch, "E53.20.5.0", {"start": v(11.1, -22.04) * mm, "mid": v(11.78, -21.08) * mm, "end": v(11.39, -19.98) * mm});
            skLineSegment(sketch, "E53.24.5.0", {"start": v(11.39, -19.98) * mm, "end": v(8.38, -17.18) * mm});
            skArc(sketch, "E53.27.5.0", {"start": v(5.67, -24.01) * mm, "mid": v(7.07, -23.64) * mm, "end": v(8.44, -23.18) * mm});
            skArc(sketch, "E53.31.5.0", {"start": v(11.1, -22.04) * mm, "mid": v(11.78, -21.08) * mm, "end": v(11.39, -19.98) * mm});
            skPoint(sketch, "E53.35.5.0", {"position": v(3.9, -24.36) * mm});
            skLineSegment(sketch, "E53.36.5.0", {"start": v(4.12, -22.62) * mm, "end": v(4.62, -18.55) * mm});
            skArc(sketch, "E53.39.5.0", {"start": v(11.1, -22.04) * mm, "mid": v(9.78, -22.65) * mm, "end": v(8.44, -23.18) * mm});
            skPoint(sketch, "E53.43.5.0", {"position": v(12.67, -21.17) * mm});
            skPoint(sketch, "E53.44.5.0", {"position": v(4.72, -17.72) * mm});
            skPoint(sketch, "E53.45.5.0", {"position": v(3.9, -24.36) * mm});
            skArc(sketch, "E53.46.5.0", {"start": v(5.67, -24.01) * mm, "mid": v(4.53, -23.72) * mm, "end": v(4.12, -22.62) * mm});
            skArc(sketch, "E53.50.5.0", {"start": v(11.1, -22.04) * mm, "mid": v(11.78, -21.08) * mm, "end": v(11.39, -19.98) * mm});
            skLineSegment(sketch, "E53.54.5.0", {"start": v(11.39, -19.98) * mm, "end": v(8.38, -17.18) * mm});
            skPoint(sketch, "E53.57.5.0", {"position": v(3.9, -24.36) * mm});
            skArc(sketch, "E53.58.5.0", {"start": v(5.67, -24.01) * mm, "mid": v(7.07, -23.64) * mm, "end": v(8.44, -23.18) * mm});
            skPoint(sketch, "E53.62.5.0", {"position": v(4.72, -17.72) * mm});
            skArc(sketch, "E53.63.5.0", {"start": v(11.1, -22.04) * mm, "mid": v(9.78, -22.65) * mm, "end": v(8.44, -23.18) * mm});
            skPoint(sketch, "E53.67.5.0", {"position": v(7.77, -16.6) * mm});
            skPoint(sketch, "E53.68.5.0", {"position": v(12.67, -21.17) * mm});
            skLineSegment(sketch, "E53.69.5.0", {"start": v(4.12, -22.62) * mm, "end": v(4.62, -18.55) * mm});
            skArc(sketch, "E53.72.5.0", {"start": v(5.67, -24.01) * mm, "mid": v(4.53, -23.72) * mm, "end": v(4.12, -22.62) * mm});
            skLineSegment(sketch, "E53.76.5.0", {"start": v(11.39, -19.98) * mm, "end": v(8.38, -17.18) * mm});
            skPoint(sketch, "E53.79.5.0", {"position": v(7.77, -16.6) * mm});
            skArc(sketch, "E53.80.5.0", {"start": v(11.1, -22.04) * mm, "mid": v(9.78, -22.65) * mm, "end": v(8.44, -23.18) * mm});
            skPoint(sketch, "E53.84.5.0", {"position": v(12.67, -21.17) * mm});
            skPoint(sketch, "E53.85.5.0", {"position": v(3.9, -24.36) * mm});
            skLineSegment(sketch, "E53.86.5.0", {"start": v(4.12, -22.62) * mm, "end": v(4.62, -18.55) * mm});
            skArc(sketch, "E53.89.5.0", {"start": v(5.67, -24.01) * mm, "mid": v(7.07, -23.64) * mm, "end": v(8.44, -23.18) * mm});
            skArc(sketch, "E53.93.5.0", {"start": v(11.1, -22.04) * mm, "mid": v(11.78, -21.08) * mm, "end": v(11.39, -19.98) * mm});
            skArc(sketch, "E53.97.5.0", {"start": v(5.67, -24.01) * mm, "mid": v(4.53, -23.72) * mm, "end": v(4.12, -22.62) * mm});
            skPoint(sketch, "E53.101.5.0", {"position": v(4.72, -17.72) * mm});
            skArc(sketch, "E53.102.5.0", {"start": v(5.67, -24.01) * mm, "mid": v(7.07, -23.64) * mm, "end": v(8.44, -23.18) * mm});
            skArc(sketch, "E53.106.5.0", {"start": v(11.1, -22.04) * mm, "mid": v(9.78, -22.65) * mm, "end": v(8.44, -23.18) * mm});
            skLineSegment(sketch, "E53.110.5.0", {"start": v(4.12, -22.62) * mm, "end": v(4.62, -18.55) * mm});
            skPoint(sketch, "E53.113.5.0", {"position": v(3.9, -24.36) * mm});
            skArc(sketch, "E53.114.5.0", {"start": v(11.1, -22.04) * mm, "mid": v(11.78, -21.08) * mm, "end": v(11.39, -19.98) * mm});
            skPoint(sketch, "E53.118.5.0", {"position": v(4.72, -17.72) * mm});
            skPoint(sketch, "E53.119.5.0", {"position": v(12.67, -21.17) * mm});
            skPoint(sketch, "E53.120.5.0", {"position": v(7.77, -16.6) * mm});
            skLineSegment(sketch, "E53.121.5.0", {"start": v(11.39, -19.98) * mm, "end": v(8.38, -17.18) * mm});
            skArc(sketch, "E53.124.5.0", {"start": v(5.67, -24.01) * mm, "mid": v(4.53, -23.72) * mm, "end": v(4.12, -22.62) * mm});
            skPoint(sketch, "E53.128.5.0", {"position": v(4.72, -17.72) * mm});
            skPoint(sketch, "E53.129.5.0", {"position": v(7.77, -16.6) * mm});
            skArc(sketch, "E53.130.5.0", {"start": v(4.62, -18.55) * mm, "mid": v(4.9, -17.9) * mm, "end": v(5.5, -17.5) * mm});
            skArc(sketch, "E53.134.5.0", {"start": v(4.62, -18.55) * mm, "mid": v(4.9, -17.9) * mm, "end": v(5.5, -17.5) * mm});
            skArc(sketch, "E53.138.5.0", {"start": v(8.38, -17.18) * mm, "mid": v(7.74, -16.86) * mm, "end": v(7.03, -16.94) * mm});
            skArc(sketch, "E53.142.5.0", {"start": v(4.62, -18.55) * mm, "mid": v(4.9, -17.9) * mm, "end": v(5.5, -17.5) * mm});
            skArc(sketch, "E53.146.5.0", {"start": v(4.62, -18.55) * mm, "mid": v(4.9, -17.9) * mm, "end": v(5.5, -17.5) * mm});
            skArc(sketch, "E53.150.5.0", {"start": v(8.38, -17.18) * mm, "mid": v(7.74, -16.86) * mm, "end": v(7.03, -16.94) * mm});
            skArc(sketch, "E53.154.5.0", {"start": v(4.62, -18.55) * mm, "mid": v(4.9, -17.9) * mm, "end": v(5.5, -17.5) * mm});
            skArc(sketch, "E53.158.5.0", {"start": v(8.38, -17.18) * mm, "mid": v(7.74, -16.86) * mm, "end": v(7.03, -16.94) * mm});
            skArc(sketch, "E53.162.5.0", {"start": v(5.5, -17.5) * mm, "mid": v(5.89, -17.37) * mm, "end": v(6.27, -17.23) * mm});
            skArc(sketch, "E53.166.5.0", {"start": v(8.38, -17.18) * mm, "mid": v(7.74, -16.86) * mm, "end": v(7.03, -16.94) * mm});
            skArc(sketch, "E53.170.5.0", {"start": v(7.03, -16.94) * mm, "mid": v(6.65, -17.09) * mm, "end": v(6.27, -17.23) * mm});
            skArc(sketch, "E53.174.5.0", {"start": v(7.03, -16.94) * mm, "mid": v(6.65, -17.09) * mm, "end": v(6.27, -17.23) * mm});
            skArc(sketch, "E53.178.5.0", {"start": v(8.38, -17.18) * mm, "mid": v(7.74, -16.86) * mm, "end": v(7.03, -16.94) * mm});
            skArc(sketch, "E53.182.5.0", {"start": v(5.5, -17.5) * mm, "mid": v(5.89, -17.37) * mm, "end": v(6.27, -17.23) * mm});
            skArc(sketch, "E53.186.5.0", {"start": v(7.03, -16.94) * mm, "mid": v(6.65, -17.09) * mm, "end": v(6.27, -17.23) * mm});
            skArc(sketch, "E53.190.5.0", {"start": v(5.5, -17.5) * mm, "mid": v(5.89, -17.37) * mm, "end": v(6.27, -17.23) * mm});
            skArc(sketch, "E53.194.5.0", {"start": v(5.5, -17.5) * mm, "mid": v(5.89, -17.37) * mm, "end": v(6.27, -17.23) * mm});
            skArc(sketch, "E53.198.5.0", {"start": v(7.03, -16.94) * mm, "mid": v(6.65, -17.09) * mm, "end": v(6.27, -17.23) * mm});
            skArc(sketch, "E53.202.5.0", {"start": v(7.03, -16.94) * mm, "mid": v(6.65, -17.09) * mm, "end": v(6.27, -17.23) * mm});
            skArc(sketch, "E53.206.5.0", {"start": v(5.5, -17.5) * mm, "mid": v(5.89, -17.37) * mm, "end": v(6.27, -17.23) * mm});
            skPoint(sketch, "E53.0.6.0", {"position": v(16.63, -7.73) * mm});
            skPoint(sketch, "E53.1.6.0", {"position": v(23.31, -8.07) * mm});
            skLineSegment(sketch, "E53.2.6.0", {"start": v(21.56, -7.98) * mm, "end": v(17.47, -7.77) * mm});
            skLineSegment(sketch, "E53.5.6.0", {"start": v(17.7, -14.68) * mm, "end": v(15.46, -11.24) * mm});
            skArc(sketch, "E53.8.6.0", {"start": v(19.78, -14.75) * mm, "mid": v(20.6, -13.57) * mm, "end": v(21.37, -12.34) * mm});
            skArc(sketch, "E53.12.6.0", {"start": v(19.78, -14.75) * mm, "mid": v(18.72, -15.26) * mm, "end": v(17.7, -14.68) * mm});
            skArc(sketch, "E53.16.6.0", {"start": v(22.66, -9.75) * mm, "mid": v(22.05, -11.06) * mm, "end": v(21.37, -12.34) * mm});
            skArc(sketch, "E53.20.6.0", {"start": v(22.66, -9.75) * mm, "mid": v(22.58, -8.58) * mm, "end": v(21.56, -7.98) * mm});
            skLineSegment(sketch, "E53.24.6.0", {"start": v(21.56, -7.98) * mm, "end": v(17.47, -7.77) * mm});
            skArc(sketch, "E53.27.6.0", {"start": v(19.78, -14.75) * mm, "mid": v(20.6, -13.57) * mm, "end": v(21.37, -12.34) * mm});
            skArc(sketch, "E53.31.6.0", {"start": v(22.66, -9.75) * mm, "mid": v(22.58, -8.58) * mm, "end": v(21.56, -7.98) * mm});
            skPoint(sketch, "E53.35.6.0", {"position": v(18.65, -16.15) * mm});
            skLineSegment(sketch, "E53.36.6.0", {"start": v(17.7, -14.68) * mm, "end": v(15.46, -11.24) * mm});
            skArc(sketch, "E53.39.6.0", {"start": v(22.66, -9.75) * mm, "mid": v(22.05, -11.06) * mm, "end": v(21.37, -12.34) * mm});
            skPoint(sketch, "E53.43.6.0", {"position": v(23.31, -8.07) * mm});
            skPoint(sketch, "E53.44.6.0", {"position": v(15, -10.54) * mm});
            skPoint(sketch, "E53.45.6.0", {"position": v(18.65, -16.15) * mm});
            skArc(sketch, "E53.46.6.0", {"start": v(19.78, -14.75) * mm, "mid": v(18.72, -15.26) * mm, "end": v(17.7, -14.68) * mm});
            skArc(sketch, "E53.50.6.0", {"start": v(22.66, -9.75) * mm, "mid": v(22.58, -8.58) * mm, "end": v(21.56, -7.98) * mm});
            skLineSegment(sketch, "E53.54.6.0", {"start": v(21.56, -7.98) * mm, "end": v(17.47, -7.77) * mm});
            skPoint(sketch, "E53.57.6.0", {"position": v(18.65, -16.15) * mm});
            skArc(sketch, "E53.58.6.0", {"start": v(19.78, -14.75) * mm, "mid": v(20.6, -13.57) * mm, "end": v(21.37, -12.34) * mm});
            skPoint(sketch, "E53.62.6.0", {"position": v(15, -10.54) * mm});
            skArc(sketch, "E53.63.6.0", {"start": v(22.66, -9.75) * mm, "mid": v(22.05, -11.06) * mm, "end": v(21.37, -12.34) * mm});
            skPoint(sketch, "E53.67.6.0", {"position": v(16.63, -7.73) * mm});
            skPoint(sketch, "E53.68.6.0", {"position": v(23.31, -8.07) * mm});
            skLineSegment(sketch, "E53.69.6.0", {"start": v(17.7, -14.68) * mm, "end": v(15.46, -11.24) * mm});
            skArc(sketch, "E53.72.6.0", {"start": v(19.78, -14.75) * mm, "mid": v(18.72, -15.26) * mm, "end": v(17.7, -14.68) * mm});
            skLineSegment(sketch, "E53.76.6.0", {"start": v(21.56, -7.98) * mm, "end": v(17.47, -7.77) * mm});
            skPoint(sketch, "E53.79.6.0", {"position": v(16.63, -7.73) * mm});
            skArc(sketch, "E53.80.6.0", {"start": v(22.66, -9.75) * mm, "mid": v(22.05, -11.06) * mm, "end": v(21.37, -12.34) * mm});
            skPoint(sketch, "E53.84.6.0", {"position": v(23.31, -8.07) * mm});
            skPoint(sketch, "E53.85.6.0", {"position": v(18.65, -16.15) * mm});
            skLineSegment(sketch, "E53.86.6.0", {"start": v(17.7, -14.68) * mm, "end": v(15.46, -11.24) * mm});
            skArc(sketch, "E53.89.6.0", {"start": v(19.78, -14.75) * mm, "mid": v(20.6, -13.57) * mm, "end": v(21.37, -12.34) * mm});
            skArc(sketch, "E53.93.6.0", {"start": v(22.66, -9.75) * mm, "mid": v(22.58, -8.58) * mm, "end": v(21.56, -7.98) * mm});
            skArc(sketch, "E53.97.6.0", {"start": v(19.78, -14.75) * mm, "mid": v(18.72, -15.26) * mm, "end": v(17.7, -14.68) * mm});
            skPoint(sketch, "E53.101.6.0", {"position": v(15, -10.54) * mm});
            skArc(sketch, "E53.102.6.0", {"start": v(19.78, -14.75) * mm, "mid": v(20.6, -13.57) * mm, "end": v(21.37, -12.34) * mm});
            skArc(sketch, "E53.106.6.0", {"start": v(22.66, -9.75) * mm, "mid": v(22.05, -11.06) * mm, "end": v(21.37, -12.34) * mm});
            skLineSegment(sketch, "E53.110.6.0", {"start": v(17.7, -14.68) * mm, "end": v(15.46, -11.24) * mm});
            skPoint(sketch, "E53.113.6.0", {"position": v(18.65, -16.15) * mm});
            skArc(sketch, "E53.114.6.0", {"start": v(22.66, -9.75) * mm, "mid": v(22.58, -8.58) * mm, "end": v(21.56, -7.98) * mm});
            skPoint(sketch, "E53.118.6.0", {"position": v(15, -10.54) * mm});
            skPoint(sketch, "E53.119.6.0", {"position": v(23.31, -8.07) * mm});
            skPoint(sketch, "E53.120.6.0", {"position": v(16.63, -7.73) * mm});
            skLineSegment(sketch, "E53.121.6.0", {"start": v(21.56, -7.98) * mm, "end": v(17.47, -7.77) * mm});
            skArc(sketch, "E53.124.6.0", {"start": v(19.78, -14.75) * mm, "mid": v(18.72, -15.26) * mm, "end": v(17.7, -14.68) * mm});
            skPoint(sketch, "E53.128.6.0", {"position": v(15, -10.54) * mm});
            skPoint(sketch, "E53.129.6.0", {"position": v(16.63, -7.73) * mm});
            skArc(sketch, "E53.130.6.0", {"start": v(15.46, -11.24) * mm, "mid": v(15.26, -10.55) * mm, "end": v(15.46, -9.87) * mm});
            skArc(sketch, "E53.134.6.0", {"start": v(15.46, -11.24) * mm, "mid": v(15.26, -10.55) * mm, "end": v(15.46, -9.87) * mm});
            skArc(sketch, "E53.138.6.0", {"start": v(17.47, -7.77) * mm, "mid": v(16.77, -7.94) * mm, "end": v(16.27, -8.45) * mm});
            skArc(sketch, "E53.142.6.0", {"start": v(15.46, -11.24) * mm, "mid": v(15.26, -10.55) * mm, "end": v(15.46, -9.87) * mm});
            skArc(sketch, "E53.146.6.0", {"start": v(15.46, -11.24) * mm, "mid": v(15.26, -10.55) * mm, "end": v(15.46, -9.87) * mm});
            skArc(sketch, "E53.150.6.0", {"start": v(17.47, -7.77) * mm, "mid": v(16.77, -7.94) * mm, "end": v(16.27, -8.45) * mm});
            skArc(sketch, "E53.154.6.0", {"start": v(15.46, -11.24) * mm, "mid": v(15.26, -10.55) * mm, "end": v(15.46, -9.87) * mm});
            skArc(sketch, "E53.158.6.0", {"start": v(17.47, -7.77) * mm, "mid": v(16.77, -7.94) * mm, "end": v(16.27, -8.45) * mm});
            skArc(sketch, "E53.162.6.0", {"start": v(15.46, -9.87) * mm, "mid": v(15.67, -9.52) * mm, "end": v(15.88, -9.17) * mm});
            skArc(sketch, "E53.166.6.0", {"start": v(17.47, -7.77) * mm, "mid": v(16.77, -7.94) * mm, "end": v(16.27, -8.45) * mm});
            skArc(sketch, "E53.170.6.0", {"start": v(16.27, -8.45) * mm, "mid": v(16.08, -8.81) * mm, "end": v(15.88, -9.17) * mm});
            skArc(sketch, "E53.174.6.0", {"start": v(16.27, -8.45) * mm, "mid": v(16.08, -8.81) * mm, "end": v(15.88, -9.17) * mm});
            skArc(sketch, "E53.178.6.0", {"start": v(17.47, -7.77) * mm, "mid": v(16.77, -7.94) * mm, "end": v(16.27, -8.45) * mm});
            skArc(sketch, "E53.182.6.0", {"start": v(15.46, -9.87) * mm, "mid": v(15.67, -9.52) * mm, "end": v(15.88, -9.17) * mm});
            skArc(sketch, "E53.186.6.0", {"start": v(16.27, -8.45) * mm, "mid": v(16.08, -8.81) * mm, "end": v(15.88, -9.17) * mm});
            skArc(sketch, "E53.190.6.0", {"start": v(15.46, -9.87) * mm, "mid": v(15.67, -9.52) * mm, "end": v(15.88, -9.17) * mm});
            skArc(sketch, "E53.194.6.0", {"start": v(15.46, -9.87) * mm, "mid": v(15.67, -9.52) * mm, "end": v(15.88, -9.17) * mm});
            skArc(sketch, "E53.198.6.0", {"start": v(16.27, -8.45) * mm, "mid": v(16.08, -8.81) * mm, "end": v(15.88, -9.17) * mm});
            skArc(sketch, "E53.202.6.0", {"start": v(16.27, -8.45) * mm, "mid": v(16.08, -8.81) * mm, "end": v(15.88, -9.17) * mm});
            skArc(sketch, "E53.206.6.0", {"start": v(15.46, -9.87) * mm, "mid": v(15.67, -9.52) * mm, "end": v(15.88, -9.17) * mm});
            skPoint(sketch, "E54.0.7.0", {"position": v(17.7, 4.77) * mm});
            skPoint(sketch, "E54.1.7.0", {"position": v(23.05, 8.8) * mm});
            skLineSegment(sketch, "E54.2.7.0", {"start": v(21.65, 7.74) * mm, "end": v(18.37, 5.27) * mm});
            skLineSegment(sketch, "E54.5.7.0", {"start": v(23, 0.13) * mm, "end": v(19.07, 1.33) * mm});
            skArc(sketch, "E54.8.7.0", {"start": v(24.63, 1.41) * mm, "mid": v(24.5, 2.85) * mm, "end": v(24.3, 4.28) * mm});
            skArc(sketch, "E54.12.7.0", {"start": v(24.63, 1.41) * mm, "mid": v(24.15, 0.34) * mm, "end": v(23, 0.13) * mm});
            skArc(sketch, "E54.16.7.0", {"start": v(23.63, 7.1) * mm, "mid": v(24, 5.7) * mm, "end": v(24.3, 4.28) * mm});
            skArc(sketch, "E54.20.7.0", {"start": v(23.63, 7.1) * mm, "mid": v(22.8, 7.94) * mm, "end": v(21.65, 7.74) * mm});
            skLineSegment(sketch, "E54.24.7.0", {"start": v(21.65, 7.74) * mm, "end": v(18.37, 5.27) * mm});
            skArc(sketch, "E54.27.7.0", {"start": v(24.63, 1.41) * mm, "mid": v(24.5, 2.85) * mm, "end": v(24.3, 4.28) * mm});
            skArc(sketch, "E54.31.7.0", {"start": v(23.63, 7.1) * mm, "mid": v(22.8, 7.94) * mm, "end": v(21.65, 7.74) * mm});
            skPoint(sketch, "E54.35.7.0", {"position": v(24.67, -0.39) * mm});
            skLineSegment(sketch, "E54.36.7.0", {"start": v(23, 0.13) * mm, "end": v(19.07, 1.33) * mm});
            skArc(sketch, "E54.39.7.0", {"start": v(23.63, 7.1) * mm, "mid": v(24, 5.7) * mm, "end": v(24.3, 4.28) * mm});
            skPoint(sketch, "E54.43.7.0", {"position": v(23.05, 8.8) * mm});
            skPoint(sketch, "E54.44.7.0", {"position": v(18.27, 1.57) * mm});
            skPoint(sketch, "E54.45.7.0", {"position": v(24.67, -0.39) * mm});
            skArc(sketch, "E54.46.7.0", {"start": v(24.63, 1.41) * mm, "mid": v(24.15, 0.34) * mm, "end": v(23, 0.13) * mm});
            skArc(sketch, "E54.50.7.0", {"start": v(23.63, 7.1) * mm, "mid": v(22.8, 7.94) * mm, "end": v(21.65, 7.74) * mm});
            skLineSegment(sketch, "E54.54.7.0", {"start": v(21.65, 7.74) * mm, "end": v(18.37, 5.27) * mm});
            skPoint(sketch, "E54.57.7.0", {"position": v(24.67, -0.39) * mm});
            skArc(sketch, "E54.58.7.0", {"start": v(24.63, 1.41) * mm, "mid": v(24.5, 2.85) * mm, "end": v(24.3, 4.28) * mm});
            skPoint(sketch, "E54.62.7.0", {"position": v(18.27, 1.57) * mm});
            skArc(sketch, "E54.63.7.0", {"start": v(23.63, 7.1) * mm, "mid": v(24, 5.7) * mm, "end": v(24.3, 4.28) * mm});
            skPoint(sketch, "E54.67.7.0", {"position": v(17.7, 4.77) * mm});
            skPoint(sketch, "E54.68.7.0", {"position": v(23.05, 8.8) * mm});
            skLineSegment(sketch, "E54.69.7.0", {"start": v(23, 0.13) * mm, "end": v(19.07, 1.33) * mm});
            skArc(sketch, "E54.72.7.0", {"start": v(24.63, 1.41) * mm, "mid": v(24.15, 0.34) * mm, "end": v(23, 0.13) * mm});
            skLineSegment(sketch, "E54.76.7.0", {"start": v(21.65, 7.74) * mm, "end": v(18.37, 5.27) * mm});
            skPoint(sketch, "E54.79.7.0", {"position": v(17.7, 4.77) * mm});
            skArc(sketch, "E54.80.7.0", {"start": v(23.63, 7.1) * mm, "mid": v(24, 5.7) * mm, "end": v(24.3, 4.28) * mm});
            skPoint(sketch, "E54.84.7.0", {"position": v(23.05, 8.8) * mm});
            skPoint(sketch, "E54.85.7.0", {"position": v(24.67, -0.39) * mm});
            skLineSegment(sketch, "E54.86.7.0", {"start": v(23, 0.13) * mm, "end": v(19.07, 1.33) * mm});
            skArc(sketch, "E54.89.7.0", {"start": v(24.63, 1.41) * mm, "mid": v(24.5, 2.85) * mm, "end": v(24.3, 4.28) * mm});
            skArc(sketch, "E54.93.7.0", {"start": v(23.63, 7.1) * mm, "mid": v(22.8, 7.94) * mm, "end": v(21.65, 7.74) * mm});
            skArc(sketch, "E54.97.7.0", {"start": v(24.63, 1.41) * mm, "mid": v(24.15, 0.34) * mm, "end": v(23, 0.13) * mm});
            skPoint(sketch, "E54.101.7.0", {"position": v(18.27, 1.57) * mm});
            skArc(sketch, "E54.102.7.0", {"start": v(24.63, 1.41) * mm, "mid": v(24.5, 2.85) * mm, "end": v(24.3, 4.28) * mm});
            skArc(sketch, "E54.106.7.0", {"start": v(23.63, 7.1) * mm, "mid": v(24, 5.7) * mm, "end": v(24.3, 4.28) * mm});
            skLineSegment(sketch, "E54.110.7.0", {"start": v(23, 0.13) * mm, "end": v(19.07, 1.33) * mm});
            skPoint(sketch, "E54.113.7.0", {"position": v(24.67, -0.39) * mm});
            skArc(sketch, "E54.114.7.0", {"start": v(23.63, 7.1) * mm, "mid": v(22.8, 7.94) * mm, "end": v(21.65, 7.74) * mm});
            skPoint(sketch, "E54.118.7.0", {"position": v(18.27, 1.57) * mm});
            skPoint(sketch, "E54.119.7.0", {"position": v(23.05, 8.8) * mm});
            skPoint(sketch, "E54.120.7.0", {"position": v(17.7, 4.77) * mm});
            skLineSegment(sketch, "E54.121.7.0", {"start": v(21.65, 7.74) * mm, "end": v(18.37, 5.27) * mm});
            skArc(sketch, "E54.124.7.0", {"start": v(24.63, 1.41) * mm, "mid": v(24.15, 0.34) * mm, "end": v(23, 0.13) * mm});
            skPoint(sketch, "E54.128.7.0", {"position": v(18.27, 1.57) * mm});
            skPoint(sketch, "E54.129.7.0", {"position": v(17.7, 4.77) * mm});
            skArc(sketch, "E54.130.7.0", {"start": v(19.07, 1.33) * mm, "mid": v(18.47, 1.72) * mm, "end": v(18.18, 2.38) * mm});
            skArc(sketch, "E54.134.7.0", {"start": v(19.07, 1.33) * mm, "mid": v(18.47, 1.72) * mm, "end": v(18.18, 2.38) * mm});
            skArc(sketch, "E54.138.7.0", {"start": v(18.37, 5.27) * mm, "mid": v(17.95, 4.7) * mm, "end": v(17.9, 3.98) * mm});
            skArc(sketch, "E54.142.7.0", {"start": v(19.07, 1.33) * mm, "mid": v(18.47, 1.72) * mm, "end": v(18.18, 2.38) * mm});
            skArc(sketch, "E54.146.7.0", {"start": v(19.07, 1.33) * mm, "mid": v(18.47, 1.72) * mm, "end": v(18.18, 2.38) * mm});
            skArc(sketch, "E54.150.7.0", {"start": v(18.37, 5.27) * mm, "mid": v(17.95, 4.7) * mm, "end": v(17.9, 3.98) * mm});
            skArc(sketch, "E54.154.7.0", {"start": v(19.07, 1.33) * mm, "mid": v(18.47, 1.72) * mm, "end": v(18.18, 2.38) * mm});
            skArc(sketch, "E54.158.7.0", {"start": v(18.37, 5.27) * mm, "mid": v(17.95, 4.7) * mm, "end": v(17.9, 3.98) * mm});
            skArc(sketch, "E54.162.7.0", {"start": v(18.18, 2.38) * mm, "mid": v(18.12, 2.78) * mm, "end": v(18.06, 3.18) * mm});
            skArc(sketch, "E54.166.7.0", {"start": v(18.37, 5.27) * mm, "mid": v(17.95, 4.7) * mm, "end": v(17.9, 3.98) * mm});
            skArc(sketch, "E54.170.7.0", {"start": v(17.9, 3.98) * mm, "mid": v(17.98, 3.59) * mm, "end": v(18.06, 3.18) * mm});
            skArc(sketch, "E54.174.7.0", {"start": v(17.9, 3.98) * mm, "mid": v(17.98, 3.59) * mm, "end": v(18.06, 3.18) * mm});
            skArc(sketch, "E54.178.7.0", {"start": v(18.37, 5.27) * mm, "mid": v(17.95, 4.7) * mm, "end": v(17.9, 3.98) * mm});
            skArc(sketch, "E54.182.7.0", {"start": v(18.18, 2.38) * mm, "mid": v(18.12, 2.78) * mm, "end": v(18.06, 3.18) * mm});
            skArc(sketch, "E54.186.7.0", {"start": v(17.9, 3.98) * mm, "mid": v(17.98, 3.59) * mm, "end": v(18.06, 3.18) * mm});
            skArc(sketch, "E54.190.7.0", {"start": v(18.18, 2.38) * mm, "mid": v(18.12, 2.78) * mm, "end": v(18.06, 3.18) * mm});
            skArc(sketch, "E54.194.7.0", {"start": v(18.18, 2.38) * mm, "mid": v(18.12, 2.78) * mm, "end": v(18.06, 3.18) * mm});
            skArc(sketch, "E54.198.7.0", {"start": v(17.9, 3.98) * mm, "mid": v(17.98, 3.59) * mm, "end": v(18.06, 3.18) * mm});
            skArc(sketch, "E54.202.7.0", {"start": v(17.9, 3.98) * mm, "mid": v(17.98, 3.59) * mm, "end": v(18.06, 3.18) * mm});
            skArc(sketch, "E54.206.7.0", {"start": v(18.18, 2.38) * mm, "mid": v(18.12, 2.78) * mm, "end": v(18.06, 3.18) * mm});
            skPoint(sketch, "E54.0.8.0", {"position": v(10.5, 15.04) * mm});
            skPoint(sketch, "E54.1.8.0", {"position": v(12, 21.56) * mm});
            skLineSegment(sketch, "E54.2.8.0", {"start": v(11.6, 19.85) * mm, "end": v(10.69, 15.85) * mm});
            skLineSegment(sketch, "E54.5.8.0", {"start": v(17.53, 14.88) * mm, "end": v(13.75, 13.28) * mm});
            skArc(sketch, "E54.8.8.0", {"start": v(17.96, 16.92) * mm, "mid": v(16.94, 17.94) * mm, "end": v(15.86, 18.9) * mm});
            skArc(sketch, "E54.12.8.0", {"start": v(17.96, 16.92) * mm, "mid": v(18.28, 15.78) * mm, "end": v(17.53, 14.88) * mm});
            skArc(sketch, "E54.16.8.0", {"start": v(13.54, 20.63) * mm, "mid": v(14.73, 19.8) * mm, "end": v(15.86, 18.9) * mm});
            skArc(sketch, "E54.20.8.0", {"start": v(13.54, 20.63) * mm, "mid": v(12.37, 20.74) * mm, "end": v(11.6, 19.85) * mm});
            skLineSegment(sketch, "E54.24.8.0", {"start": v(11.6, 19.85) * mm, "end": v(10.69, 15.85) * mm});
            skArc(sketch, "E54.27.8.0", {"start": v(17.96, 16.92) * mm, "mid": v(16.94, 17.94) * mm, "end": v(15.86, 18.9) * mm});
            skArc(sketch, "E54.31.8.0", {"start": v(13.54, 20.63) * mm, "mid": v(12.37, 20.74) * mm, "end": v(11.6, 19.85) * mm});
            skPoint(sketch, "E54.35.8.0", {"position": v(19.15, 15.56) * mm});
            skLineSegment(sketch, "E54.36.8.0", {"start": v(17.53, 14.88) * mm, "end": v(13.75, 13.28) * mm});
            skArc(sketch, "E54.39.8.0", {"start": v(13.54, 20.63) * mm, "mid": v(14.73, 19.8) * mm, "end": v(15.86, 18.9) * mm});
            skPoint(sketch, "E54.43.8.0", {"position": v(12, 21.56) * mm});
            skPoint(sketch, "E54.44.8.0", {"position": v(12.98, 12.95) * mm});
            skPoint(sketch, "E54.45.8.0", {"position": v(19.15, 15.56) * mm});
            skArc(sketch, "E54.46.8.0", {"start": v(17.96, 16.92) * mm, "mid": v(18.28, 15.78) * mm, "end": v(17.53, 14.88) * mm});
            skArc(sketch, "E54.50.8.0", {"start": v(13.54, 20.63) * mm, "mid": v(12.37, 20.74) * mm, "end": v(11.6, 19.85) * mm});
            skLineSegment(sketch, "E54.54.8.0", {"start": v(11.6, 19.85) * mm, "end": v(10.69, 15.85) * mm});
            skPoint(sketch, "E54.57.8.0", {"position": v(19.15, 15.56) * mm});
            skArc(sketch, "E54.58.8.0", {"start": v(17.96, 16.92) * mm, "mid": v(16.94, 17.94) * mm, "end": v(15.86, 18.9) * mm});
            skPoint(sketch, "E54.62.8.0", {"position": v(12.98, 12.95) * mm});
            skArc(sketch, "E54.63.8.0", {"start": v(13.54, 20.63) * mm, "mid": v(14.73, 19.8) * mm, "end": v(15.86, 18.9) * mm});
            skPoint(sketch, "E54.67.8.0", {"position": v(10.5, 15.04) * mm});
            skPoint(sketch, "E54.68.8.0", {"position": v(12, 21.56) * mm});
            skLineSegment(sketch, "E54.69.8.0", {"start": v(17.53, 14.88) * mm, "end": v(13.75, 13.28) * mm});
            skArc(sketch, "E54.72.8.0", {"start": v(17.96, 16.92) * mm, "mid": v(18.28, 15.78) * mm, "end": v(17.53, 14.88) * mm});
            skLineSegment(sketch, "E54.76.8.0", {"start": v(11.6, 19.85) * mm, "end": v(10.69, 15.85) * mm});
            skPoint(sketch, "E54.79.8.0", {"position": v(10.5, 15.04) * mm});
            skArc(sketch, "E54.80.8.0", {"start": v(13.54, 20.63) * mm, "mid": v(14.73, 19.8) * mm, "end": v(15.86, 18.9) * mm});
            skPoint(sketch, "E54.84.8.0", {"position": v(12, 21.56) * mm});
            skPoint(sketch, "E54.85.8.0", {"position": v(19.15, 15.56) * mm});
            skLineSegment(sketch, "E54.86.8.0", {"start": v(17.53, 14.88) * mm, "end": v(13.75, 13.28) * mm});
            skArc(sketch, "E54.89.8.0", {"start": v(17.96, 16.92) * mm, "mid": v(16.94, 17.94) * mm, "end": v(15.86, 18.9) * mm});
            skArc(sketch, "E54.93.8.0", {"start": v(13.54, 20.63) * mm, "mid": v(12.37, 20.74) * mm, "end": v(11.6, 19.85) * mm});
            skArc(sketch, "E54.97.8.0", {"start": v(17.96, 16.92) * mm, "mid": v(18.28, 15.78) * mm, "end": v(17.53, 14.88) * mm});
            skPoint(sketch, "E54.101.8.0", {"position": v(12.98, 12.95) * mm});
            skArc(sketch, "E54.102.8.0", {"start": v(17.96, 16.92) * mm, "mid": v(16.94, 17.94) * mm, "end": v(15.86, 18.9) * mm});
            skArc(sketch, "E54.106.8.0", {"start": v(13.54, 20.63) * mm, "mid": v(14.73, 19.8) * mm, "end": v(15.86, 18.9) * mm});
            skLineSegment(sketch, "E54.110.8.0", {"start": v(17.53, 14.88) * mm, "end": v(13.75, 13.28) * mm});
            skPoint(sketch, "E54.113.8.0", {"position": v(19.15, 15.56) * mm});
            skArc(sketch, "E54.114.8.0", {"start": v(13.54, 20.63) * mm, "mid": v(12.37, 20.74) * mm, "end": v(11.6, 19.85) * mm});
            skPoint(sketch, "E54.118.8.0", {"position": v(12.98, 12.95) * mm});
            skPoint(sketch, "E54.119.8.0", {"position": v(12, 21.56) * mm});
            skPoint(sketch, "E54.120.8.0", {"position": v(10.5, 15.04) * mm});
            skLineSegment(sketch, "E54.121.8.0", {"start": v(11.6, 19.85) * mm, "end": v(10.69, 15.85) * mm});
            skArc(sketch, "E54.124.8.0", {"start": v(17.96, 16.92) * mm, "mid": v(18.28, 15.78) * mm, "end": v(17.53, 14.88) * mm});
            skPoint(sketch, "E54.128.8.0", {"position": v(12.98, 12.95) * mm});
            skPoint(sketch, "E54.129.8.0", {"position": v(10.5, 15.04) * mm});
            skArc(sketch, "E54.130.8.0", {"start": v(13.75, 13.28) * mm, "mid": v(13.04, 13.2) * mm, "end": v(12.4, 13.5) * mm});
            skArc(sketch, "E54.134.8.0", {"start": v(13.75, 13.28) * mm, "mid": v(13.04, 13.2) * mm, "end": v(12.4, 13.5) * mm});
            skArc(sketch, "E54.138.8.0", {"start": v(10.69, 15.85) * mm, "mid": v(10.73, 15.14) * mm, "end": v(11.15, 14.56) * mm});
            skArc(sketch, "E54.142.8.0", {"start": v(13.75, 13.28) * mm, "mid": v(13.04, 13.2) * mm, "end": v(12.4, 13.5) * mm});
            skArc(sketch, "E54.146.8.0", {"start": v(13.75, 13.28) * mm, "mid": v(13.04, 13.2) * mm, "end": v(12.4, 13.5) * mm});
            skArc(sketch, "E54.150.8.0", {"start": v(10.69, 15.85) * mm, "mid": v(10.73, 15.14) * mm, "end": v(11.15, 14.56) * mm});
            skArc(sketch, "E54.154.8.0", {"start": v(13.75, 13.28) * mm, "mid": v(13.04, 13.2) * mm, "end": v(12.4, 13.5) * mm});
            skArc(sketch, "E54.158.8.0", {"start": v(10.69, 15.85) * mm, "mid": v(10.73, 15.14) * mm, "end": v(11.15, 14.56) * mm});
            skArc(sketch, "E54.162.8.0", {"start": v(12.4, 13.5) * mm, "mid": v(12.1, 13.78) * mm, "end": v(11.79, 14.05) * mm});
            skArc(sketch, "E54.166.8.0", {"start": v(10.69, 15.85) * mm, "mid": v(10.73, 15.14) * mm, "end": v(11.15, 14.56) * mm});
            skArc(sketch, "E54.170.8.0", {"start": v(11.15, 14.56) * mm, "mid": v(11.47, 14.3) * mm, "end": v(11.79, 14.05) * mm});
            skArc(sketch, "E54.174.8.0", {"start": v(11.15, 14.56) * mm, "mid": v(11.47, 14.3) * mm, "end": v(11.79, 14.05) * mm});
            skArc(sketch, "E54.178.8.0", {"start": v(10.69, 15.85) * mm, "mid": v(10.73, 15.14) * mm, "end": v(11.15, 14.56) * mm});
            skArc(sketch, "E54.182.8.0", {"start": v(12.4, 13.5) * mm, "mid": v(12.1, 13.78) * mm, "end": v(11.79, 14.05) * mm});
            skArc(sketch, "E54.186.8.0", {"start": v(11.15, 14.56) * mm, "mid": v(11.47, 14.3) * mm, "end": v(11.79, 14.05) * mm});
            skArc(sketch, "E54.190.8.0", {"start": v(12.4, 13.5) * mm, "mid": v(12.1, 13.78) * mm, "end": v(11.79, 14.05) * mm});
            skArc(sketch, "E54.194.8.0", {"start": v(12.4, 13.5) * mm, "mid": v(12.1, 13.78) * mm, "end": v(11.79, 14.05) * mm});
            skArc(sketch, "E54.198.8.0", {"start": v(11.15, 14.56) * mm, "mid": v(11.47, 14.3) * mm, "end": v(11.79, 14.05) * mm});
            skArc(sketch, "E54.202.8.0", {"start": v(11.15, 14.56) * mm, "mid": v(11.47, 14.3) * mm, "end": v(11.79, 14.05) * mm});
            skArc(sketch, "E54.206.8.0", {"start": v(12.4, 13.5) * mm, "mid": v(12.1, 13.78) * mm, "end": v(11.79, 14.05) * mm});
            skSolve(sketch);
        }
        {
            var Q0;
            Q0 = qSketchRegion(id + "F0", true);
            extrude(context, id + "F1", {"entities" : qUnion([Q0]), "depth" : 7 * mm, "offsetDistance" : 25.4 * mm});
        }
        {
            var Q0;
            Q0=makeQuery(id+"F1.opExtrude","CAP_FACE",FACE,{"disambiguationData":[OSD([sQuery(id+"F0.wireOp",EDGE,"E0"),sQuery(id+"F0.wireOp",EDGE,"E4"),sQuery(id+"F0.wireOp",EDGE,"E7.1.0"),sQuery(id+"F0.wireOp",EDGE,"E7.2.0"),sQuery(id+"F0.wireOp",EDGE,"E7.3.0"),sQuery(id+"F0.wireOp",EDGE,"E7.4.0"),sQuery(id+"F0.wireOp",EDGE,"E7.5.0"),sQuery(id+"F0.wireOp",EDGE,"E7.6.0"),sQuery(id+"F0.wireOp",EDGE,"E7.7.0"),sQuery(id+"F0.wireOp",EDGE,"E7.8.0"),sQuery(id+"F0.wireOp",EDGE,"E7.9.0"),sQuery(id+"F0.wireOp",EDGE,"E7.10.0"),sQuery(id+"F0.wireOp",EDGE,"E7.11.0"),sQuery(id+"F0.wireOp",EDGE,"E7.12.0"),sQuery(id+"F0.wireOp",EDGE,"E7.13.0"),sQuery(id+"F0.wireOp",EDGE,"E7.14.0"),sQuery(id+"F0.wireOp",EDGE,"E7.15.0"),sQuery(id+"F0.wireOp",EDGE,"E7.16.0"),sQuery(id+"F0.wireOp",EDGE,"E7.17.0"),sQuery(id+"F0.wireOp",EDGE,"E7.18.0"),sQuery(id+"F0.wireOp",EDGE,"E7.19.0"),sQuery(id+"F0.wireOp",EDGE,"E7.20.0"),sQuery(id+"F0.wireOp",EDGE,"E7.21.0"),sQuery(id+"F0.wireOp",EDGE,"E7.22.0"),sQuery(id+"F0.wireOp",EDGE,"E7.23.0"),sQuery(id+"F0.wireOp",EDGE,"E7.24.0"),sQuery(id+"F0.wireOp",EDGE,"E7.25.0"),sQuery(id+"F0.wireOp",EDGE,"E7.26.0"),sQuery(id+"F0.wireOp",EDGE,"E7.27.0"),sQuery(id+"F0.wireOp",EDGE,"E7.28.0"),sQuery(id+"F0.wireOp",EDGE,"E7.29.0"),sQuery(id+"F0.wireOp",EDGE,"E8.trimOffspring"),sQuery(id+"F0.wireOp",EDGE,"E9.trimOffspring"),sQuery(id+"F0.wireOp",EDGE,"E10.trimOffspring"),sQuery(id+"F0.wireOp",EDGE,"E11.trimOffspring"),sQuery(id+"F0.wireOp",EDGE,"E12.trimOffspring"),sQuery(id+"F0.wireOp",EDGE,"E13.trimOffspring"),sQuery(id+"F0.wireOp",EDGE,"E14.trimOffspring"),sQuery(id+"F0.wireOp",EDGE,"E15.trimOffspring"),sQuery(id+"F0.wireOp",EDGE,"E16.trimOffspring"),sQuery(id+"F0.wireOp",EDGE,"E17.trimOffspring"),sQuery(id+"F0.wireOp",EDGE,"E18.trimOffspring"),sQuery(id+"F0.wireOp",EDGE,"E19.trimOffspring"),sQuery(id+"F0.wireOp",EDGE,"E20.trimOffspring"),sQuery(id+"F0.wireOp",EDGE,"E21.trimOffspring"),sQuery(id+"F0.wireOp",EDGE,"E22.trimOffspring"),sQuery(id+"F0.wireOp",EDGE,"E23.trimOffspring"),sQuery(id+"F0.wireOp",EDGE,"E24.trimOffspring"),sQuery(id+"F0.wireOp",EDGE,"E25.trimOffspring"),sQuery(id+"F0.wireOp",EDGE,"E26.trimOffspring"),sQuery(id+"F0.wireOp",EDGE,"E27.trimOffspring"),sQuery(id+"F0.wireOp",EDGE,"E28.trimOffspring"),sQuery(id+"F0.wireOp",EDGE,"E29.trimOffspring"),sQuery(id+"F0.wireOp",EDGE,"E30.trimOffspring"),sQuery(id+"F0.wireOp",EDGE,"E31.trimOffspring"),sQuery(id+"F0.wireOp",EDGE,"E32.trimOffspring"),sQuery(id+"F0.wireOp",EDGE,"E33.trimOffspring"),sQuery(id+"F0.wireOp",EDGE,"E34.trimOffspring"),sQuery(id+"F0.wireOp",EDGE,"E35.trimOffspring"),sQuery(id+"F0.wireOp",EDGE,"E36.trimOffspring"),sQuery(id+"F0.wireOp",EDGE,"E47.MirrorCS"),sQuery(id+"F0.wireOp",EDGE,"E45.MirrorCS"),sQuery(id+"F0.wireOp",EDGE,"E40"),sQuery(id+"F0.wireOp",EDGE,"E38"),sQuery(id+"F0.wireOp",EDGE,"E46.MirrorCS"),sQuery(id+"F0.wireOp",EDGE,"E41.filletArc"),sQuery(id+"F0.wireOp",EDGE,"E48.MirrorCS"),sQuery(id+"F0.wireOp",EDGE,"E42.filletArc"),sQuery(id+"F0.wireOp",EDGE,"E39"),sQuery(id+"F0.wireOp",EDGE,"E49.MirrorCS"),sQuery(id+"F0.wireOp",EDGE,"E51.1.38"),sQuery(id+"F0.wireOp",EDGE,"E51.1.39"),sQuery(id+"F0.wireOp",EDGE,"E51.1.40"),sQuery(id+"F0.wireOp",EDGE,"E51.1.42"),sQuery(id+"F0.wireOp",EDGE,"E51.1.46"),sQuery(id+"F0.wireOp",EDGE,"E51.1.47"),sQuery(id+"F0.wireOp",EDGE,"E51.1.56"),sQuery(id+"F0.wireOp",EDGE,"E51.1.62"),sQuery(id+"F0.wireOp",EDGE,"E51.1.68"),sQuery(id+"F0.wireOp",EDGE,"E51.1.69"),sQuery(id+"F0.wireOp",EDGE,"E51.2.38"),sQuery(id+"F0.wireOp",EDGE,"E51.2.39"),sQuery(id+"F0.wireOp",EDGE,"E51.2.40"),sQuery(id+"F0.wireOp",EDGE,"E51.2.42"),sQuery(id+"F0.wireOp",EDGE,"E51.2.46"),sQuery(id+"F0.wireOp",EDGE,"E51.2.47"),sQuery(id+"F0.wireOp",EDGE,"E51.2.56"),sQuery(id+"F0.wireOp",EDGE,"E51.2.62"),sQuery(id+"F0.wireOp",EDGE,"E51.2.68"),sQuery(id+"F0.wireOp",EDGE,"E51.2.69"),sQuery(id+"F0.wireOp",EDGE,"E52.102.3.0"),sQuery(id+"F0.wireOp",EDGE,"E52.106.3.0"),sQuery(id+"F0.wireOp",EDGE,"E52.110.3.0"),sQuery(id+"F0.wireOp",EDGE,"E52.114.3.0"),sQuery(id+"F0.wireOp",EDGE,"E52.121.3.0"),sQuery(id+"F0.wireOp",EDGE,"E52.124.3.0"),sQuery(id+"F0.wireOp",EDGE,"E52.154.3.0"),sQuery(id+"F0.wireOp",EDGE,"E52.178.3.0"),sQuery(id+"F0.wireOp",EDGE,"E52.202.3.0"),sQuery(id+"F0.wireOp",EDGE,"E52.206.3.0"),sQuery(id+"F0.wireOp",EDGE,"E52.102.4.0"),sQuery(id+"F0.wireOp",EDGE,"E52.106.4.0"),sQuery(id+"F0.wireOp",EDGE,"E52.110.4.0"),sQuery(id+"F0.wireOp",EDGE,"E52.114.4.0"),sQuery(id+"F0.wireOp",EDGE,"E52.121.4.0"),sQuery(id+"F0.wireOp",EDGE,"E52.124.4.0"),sQuery(id+"F0.wireOp",EDGE,"E52.154.4.0"),sQuery(id+"F0.wireOp",EDGE,"E52.178.4.0"),sQuery(id+"F0.wireOp",EDGE,"E52.202.4.0"),sQuery(id+"F0.wireOp",EDGE,"E52.206.4.0"),sQuery(id+"F0.wireOp",EDGE,"E53.102.5.0"),sQuery(id+"F0.wireOp",EDGE,"E53.106.5.0"),sQuery(id+"F0.wireOp",EDGE,"E53.110.5.0"),sQuery(id+"F0.wireOp",EDGE,"E53.114.5.0"),sQuery(id+"F0.wireOp",EDGE,"E53.121.5.0"),sQuery(id+"F0.wireOp",EDGE,"E53.124.5.0"),sQuery(id+"F0.wireOp",EDGE,"E53.154.5.0"),sQuery(id+"F0.wireOp",EDGE,"E53.178.5.0"),sQuery(id+"F0.wireOp",EDGE,"E53.202.5.0"),sQuery(id+"F0.wireOp",EDGE,"E53.206.5.0"),sQuery(id+"F0.wireOp",EDGE,"E53.102.6.0"),sQuery(id+"F0.wireOp",EDGE,"E53.106.6.0"),sQuery(id+"F0.wireOp",EDGE,"E53.110.6.0"),sQuery(id+"F0.wireOp",EDGE,"E53.114.6.0"),sQuery(id+"F0.wireOp",EDGE,"E53.121.6.0"),sQuery(id+"F0.wireOp",EDGE,"E53.124.6.0"),sQuery(id+"F0.wireOp",EDGE,"E53.154.6.0"),sQuery(id+"F0.wireOp",EDGE,"E53.178.6.0"),sQuery(id+"F0.wireOp",EDGE,"E53.202.6.0"),sQuery(id+"F0.wireOp",EDGE,"E53.206.6.0"),sQuery(id+"F0.wireOp",EDGE,"E54.102.7.0"),sQuery(id+"F0.wireOp",EDGE,"E54.106.7.0"),sQuery(id+"F0.wireOp",EDGE,"E54.110.7.0"),sQuery(id+"F0.wireOp",EDGE,"E54.114.7.0"),sQuery(id+"F0.wireOp",EDGE,"E54.121.7.0"),sQuery(id+"F0.wireOp",EDGE,"E54.124.7.0"),sQuery(id+"F0.wireOp",EDGE,"E54.154.7.0"),sQuery(id+"F0.wireOp",EDGE,"E54.178.7.0"),sQuery(id+"F0.wireOp",EDGE,"E54.202.7.0"),sQuery(id+"F0.wireOp",EDGE,"E54.206.7.0"),sQuery(id+"F0.wireOp",EDGE,"E54.102.8.0"),sQuery(id+"F0.wireOp",EDGE,"E54.106.8.0"),sQuery(id+"F0.wireOp",EDGE,"E54.110.8.0"),sQuery(id+"F0.wireOp",EDGE,"E54.114.8.0"),sQuery(id+"F0.wireOp",EDGE,"E54.121.8.0"),sQuery(id+"F0.wireOp",EDGE,"E54.124.8.0"),sQuery(id+"F0.wireOp",EDGE,"E54.154.8.0"),sQuery(id+"F0.wireOp",EDGE,"E54.178.8.0"),sQuery(id+"F0.wireOp",EDGE,"E54.202.8.0"),sQuery(id+"F0.wireOp",EDGE,"E54.206.8.0")])],"isStart":false});
            var sketch = newSketch(context, id + "F2", { "sketchPlane" : qUnion([Q0])});
            skPoint(sketch, "E55.0.midPoint", {"position": v(-4.88, 0) * mm});
            skCircle(sketch, "E56", {"center": v(0, 0) * mm, "radius": 6.55 * mm});
            skSolve(sketch);
        }
        {
            var Q0;
            Q0 = qSketchRegion(id + "F2", true);
            extrude(context, id + "F3", {"entities" : qUnion([Q0]), "operationType" : NewBodyOperationType.REMOVE, "endBound" : BoundingType.THROUGH_ALL, "oppositeDirection" : true, "depth" : 25.4 * mm, "offsetDistance" : 25.4 * mm});
        }
        {
            var Q0;
            Q0=makeQuery(id+"F1.opExtrude","CAP_FACE",FACE,{"disambiguationData":[OSD([sQuery(id+"F0.wireOp",EDGE,"E0"),sQuery(id+"F0.wireOp",EDGE,"E4"),sQuery(id+"F0.wireOp",EDGE,"E7.1.0"),sQuery(id+"F0.wireOp",EDGE,"E7.2.0"),sQuery(id+"F0.wireOp",EDGE,"E7.3.0"),sQuery(id+"F0.wireOp",EDGE,"E7.4.0"),sQuery(id+"F0.wireOp",EDGE,"E7.5.0"),sQuery(id+"F0.wireOp",EDGE,"E7.6.0"),sQuery(id+"F0.wireOp",EDGE,"E7.7.0"),sQuery(id+"F0.wireOp",EDGE,"E7.8.0"),sQuery(id+"F0.wireOp",EDGE,"E7.9.0"),sQuery(id+"F0.wireOp",EDGE,"E7.10.0"),sQuery(id+"F0.wireOp",EDGE,"E7.11.0"),sQuery(id+"F0.wireOp",EDGE,"E7.12.0"),sQuery(id+"F0.wireOp",EDGE,"E7.13.0"),sQuery(id+"F0.wireOp",EDGE,"E7.14.0"),sQuery(id+"F0.wireOp",EDGE,"E7.15.0"),sQuery(id+"F0.wireOp",EDGE,"E7.16.0"),sQuery(id+"F0.wireOp",EDGE,"E7.17.0"),sQuery(id+"F0.wireOp",EDGE,"E7.18.0"),sQuery(id+"F0.wireOp",EDGE,"E7.19.0"),sQuery(id+"F0.wireOp",EDGE,"E7.20.0"),sQuery(id+"F0.wireOp",EDGE,"E7.21.0"),sQuery(id+"F0.wireOp",EDGE,"E7.22.0"),sQuery(id+"F0.wireOp",EDGE,"E7.23.0"),sQuery(id+"F0.wireOp",EDGE,"E7.24.0"),sQuery(id+"F0.wireOp",EDGE,"E7.25.0"),sQuery(id+"F0.wireOp",EDGE,"E7.26.0"),sQuery(id+"F0.wireOp",EDGE,"E7.27.0"),sQuery(id+"F0.wireOp",EDGE,"E7.28.0"),sQuery(id+"F0.wireOp",EDGE,"E7.29.0"),sQuery(id+"F0.wireOp",EDGE,"E8.trimOffspring"),sQuery(id+"F0.wireOp",EDGE,"E9.trimOffspring"),sQuery(id+"F0.wireOp",EDGE,"E10.trimOffspring"),sQuery(id+"F0.wireOp",EDGE,"E11.trimOffspring"),sQuery(id+"F0.wireOp",EDGE,"E12.trimOffspring"),sQuery(id+"F0.wireOp",EDGE,"E13.trimOffspring"),sQuery(id+"F0.wireOp",EDGE,"E14.trimOffspring"),sQuery(id+"F0.wireOp",EDGE,"E15.trimOffspring"),sQuery(id+"F0.wireOp",EDGE,"E16.trimOffspring"),sQuery(id+"F0.wireOp",EDGE,"E17.trimOffspring"),sQuery(id+"F0.wireOp",EDGE,"E18.trimOffspring"),sQuery(id+"F0.wireOp",EDGE,"E19.trimOffspring"),sQuery(id+"F0.wireOp",EDGE,"E20.trimOffspring"),sQuery(id+"F0.wireOp",EDGE,"E21.trimOffspring"),sQuery(id+"F0.wireOp",EDGE,"E22.trimOffspring"),sQuery(id+"F0.wireOp",EDGE,"E23.trimOffspring"),sQuery(id+"F0.wireOp",EDGE,"E24.trimOffspring"),sQuery(id+"F0.wireOp",EDGE,"E25.trimOffspring"),sQuery(id+"F0.wireOp",EDGE,"E26.trimOffspring"),sQuery(id+"F0.wireOp",EDGE,"E27.trimOffspring"),sQuery(id+"F0.wireOp",EDGE,"E28.trimOffspring"),sQuery(id+"F0.wireOp",EDGE,"E29.trimOffspring"),sQuery(id+"F0.wireOp",EDGE,"E30.trimOffspring"),sQuery(id+"F0.wireOp",EDGE,"E31.trimOffspring"),sQuery(id+"F0.wireOp",EDGE,"E32.trimOffspring"),sQuery(id+"F0.wireOp",EDGE,"E33.trimOffspring"),sQuery(id+"F0.wireOp",EDGE,"E34.trimOffspring"),sQuery(id+"F0.wireOp",EDGE,"E35.trimOffspring"),sQuery(id+"F0.wireOp",EDGE,"E36.trimOffspring"),sQuery(id+"F0.wireOp",EDGE,"E47.MirrorCS"),sQuery(id+"F0.wireOp",EDGE,"E45.MirrorCS"),sQuery(id+"F0.wireOp",EDGE,"E40"),sQuery(id+"F0.wireOp",EDGE,"E38"),sQuery(id+"F0.wireOp",EDGE,"E46.MirrorCS"),sQuery(id+"F0.wireOp",EDGE,"E41.filletArc"),sQuery(id+"F0.wireOp",EDGE,"E48.MirrorCS"),sQuery(id+"F0.wireOp",EDGE,"E42.filletArc"),sQuery(id+"F0.wireOp",EDGE,"E39"),sQuery(id+"F0.wireOp",EDGE,"E49.MirrorCS"),sQuery(id+"F0.wireOp",EDGE,"E51.1.38"),sQuery(id+"F0.wireOp",EDGE,"E51.1.39"),sQuery(id+"F0.wireOp",EDGE,"E51.1.40"),sQuery(id+"F0.wireOp",EDGE,"E51.1.42"),sQuery(id+"F0.wireOp",EDGE,"E51.1.46"),sQuery(id+"F0.wireOp",EDGE,"E51.1.47"),sQuery(id+"F0.wireOp",EDGE,"E51.1.56"),sQuery(id+"F0.wireOp",EDGE,"E51.1.62"),sQuery(id+"F0.wireOp",EDGE,"E51.1.68"),sQuery(id+"F0.wireOp",EDGE,"E51.1.69"),sQuery(id+"F0.wireOp",EDGE,"E51.2.38"),sQuery(id+"F0.wireOp",EDGE,"E51.2.39"),sQuery(id+"F0.wireOp",EDGE,"E51.2.40"),sQuery(id+"F0.wireOp",EDGE,"E51.2.42"),sQuery(id+"F0.wireOp",EDGE,"E51.2.46"),sQuery(id+"F0.wireOp",EDGE,"E51.2.47"),sQuery(id+"F0.wireOp",EDGE,"E51.2.56"),sQuery(id+"F0.wireOp",EDGE,"E51.2.62"),sQuery(id+"F0.wireOp",EDGE,"E51.2.68"),sQuery(id+"F0.wireOp",EDGE,"E51.2.69"),sQuery(id+"F0.wireOp",EDGE,"E52.102.3.0"),sQuery(id+"F0.wireOp",EDGE,"E52.106.3.0"),sQuery(id+"F0.wireOp",EDGE,"E52.110.3.0"),sQuery(id+"F0.wireOp",EDGE,"E52.114.3.0"),sQuery(id+"F0.wireOp",EDGE,"E52.121.3.0"),sQuery(id+"F0.wireOp",EDGE,"E52.124.3.0"),sQuery(id+"F0.wireOp",EDGE,"E52.154.3.0"),sQuery(id+"F0.wireOp",EDGE,"E52.178.3.0"),sQuery(id+"F0.wireOp",EDGE,"E52.202.3.0"),sQuery(id+"F0.wireOp",EDGE,"E52.206.3.0"),sQuery(id+"F0.wireOp",EDGE,"E52.102.4.0"),sQuery(id+"F0.wireOp",EDGE,"E52.106.4.0"),sQuery(id+"F0.wireOp",EDGE,"E52.110.4.0"),sQuery(id+"F0.wireOp",EDGE,"E52.114.4.0"),sQuery(id+"F0.wireOp",EDGE,"E52.121.4.0"),sQuery(id+"F0.wireOp",EDGE,"E52.124.4.0"),sQuery(id+"F0.wireOp",EDGE,"E52.154.4.0"),sQuery(id+"F0.wireOp",EDGE,"E52.178.4.0"),sQuery(id+"F0.wireOp",EDGE,"E52.202.4.0"),sQuery(id+"F0.wireOp",EDGE,"E52.206.4.0"),sQuery(id+"F0.wireOp",EDGE,"E53.102.5.0"),sQuery(id+"F0.wireOp",EDGE,"E53.106.5.0"),sQuery(id+"F0.wireOp",EDGE,"E53.110.5.0"),sQuery(id+"F0.wireOp",EDGE,"E53.114.5.0"),sQuery(id+"F0.wireOp",EDGE,"E53.121.5.0"),sQuery(id+"F0.wireOp",EDGE,"E53.124.5.0"),sQuery(id+"F0.wireOp",EDGE,"E53.154.5.0"),sQuery(id+"F0.wireOp",EDGE,"E53.178.5.0"),sQuery(id+"F0.wireOp",EDGE,"E53.202.5.0"),sQuery(id+"F0.wireOp",EDGE,"E53.206.5.0"),sQuery(id+"F0.wireOp",EDGE,"E53.102.6.0"),sQuery(id+"F0.wireOp",EDGE,"E53.106.6.0"),sQuery(id+"F0.wireOp",EDGE,"E53.110.6.0"),sQuery(id+"F0.wireOp",EDGE,"E53.114.6.0"),sQuery(id+"F0.wireOp",EDGE,"E53.121.6.0"),sQuery(id+"F0.wireOp",EDGE,"E53.124.6.0"),sQuery(id+"F0.wireOp",EDGE,"E53.154.6.0"),sQuery(id+"F0.wireOp",EDGE,"E53.178.6.0"),sQuery(id+"F0.wireOp",EDGE,"E53.202.6.0"),sQuery(id+"F0.wireOp",EDGE,"E53.206.6.0"),sQuery(id+"F0.wireOp",EDGE,"E54.102.7.0"),sQuery(id+"F0.wireOp",EDGE,"E54.106.7.0"),sQuery(id+"F0.wireOp",EDGE,"E54.110.7.0"),sQuery(id+"F0.wireOp",EDGE,"E54.114.7.0"),sQuery(id+"F0.wireOp",EDGE,"E54.121.7.0"),sQuery(id+"F0.wireOp",EDGE,"E54.124.7.0"),sQuery(id+"F0.wireOp",EDGE,"E54.154.7.0"),sQuery(id+"F0.wireOp",EDGE,"E54.178.7.0"),sQuery(id+"F0.wireOp",EDGE,"E54.202.7.0"),sQuery(id+"F0.wireOp",EDGE,"E54.206.7.0"),sQuery(id+"F0.wireOp",EDGE,"E54.102.8.0"),sQuery(id+"F0.wireOp",EDGE,"E54.106.8.0"),sQuery(id+"F0.wireOp",EDGE,"E54.110.8.0"),sQuery(id+"F0.wireOp",EDGE,"E54.114.8.0"),sQuery(id+"F0.wireOp",EDGE,"E54.121.8.0"),sQuery(id+"F0.wireOp",EDGE,"E54.124.8.0"),sQuery(id+"F0.wireOp",EDGE,"E54.154.8.0"),sQuery(id+"F0.wireOp",EDGE,"E54.178.8.0"),sQuery(id+"F0.wireOp",EDGE,"E54.202.8.0"),sQuery(id+"F0.wireOp",EDGE,"E54.206.8.0")])],"isStart":false});
            var sketch = newSketch(context, id + "F4", { "sketchPlane" : qUnion([Q0])});
            skCircle(sketch, "E57", {"center": v(0, 0) * mm, "radius": 6.55 * mm});
            skSolve(sketch);
        }
        {
            var Q0;
            Q0 = qSketchRegion(id + "F4", true);
            extrude(context, id + "F5", {"entities" : qUnion([Q0]), "operationType" : NewBodyOperationType.REMOVE, "oppositeDirection" : true, "depth" : 0.64 * mm, "offsetDistance" : 25.4 * mm});
        }
        {
            var Q0;
            Q0=makeQuery(id+"F1.opExtrude","CAP_FACE",FACE,{"disambiguationData":[OSD([sQuery(id+"F0.wireOp",EDGE,"E0"),sQuery(id+"F0.wireOp",EDGE,"E4"),sQuery(id+"F0.wireOp",EDGE,"E7.1.0"),sQuery(id+"F0.wireOp",EDGE,"E7.2.0"),sQuery(id+"F0.wireOp",EDGE,"E7.3.0"),sQuery(id+"F0.wireOp",EDGE,"E7.4.0"),sQuery(id+"F0.wireOp",EDGE,"E7.5.0"),sQuery(id+"F0.wireOp",EDGE,"E7.6.0"),sQuery(id+"F0.wireOp",EDGE,"E7.7.0"),sQuery(id+"F0.wireOp",EDGE,"E7.8.0"),sQuery(id+"F0.wireOp",EDGE,"E7.9.0"),sQuery(id+"F0.wireOp",EDGE,"E7.10.0"),sQuery(id+"F0.wireOp",EDGE,"E7.11.0"),sQuery(id+"F0.wireOp",EDGE,"E7.12.0"),sQuery(id+"F0.wireOp",EDGE,"E7.13.0"),sQuery(id+"F0.wireOp",EDGE,"E7.14.0"),sQuery(id+"F0.wireOp",EDGE,"E7.15.0"),sQuery(id+"F0.wireOp",EDGE,"E7.16.0"),sQuery(id+"F0.wireOp",EDGE,"E7.17.0"),sQuery(id+"F0.wireOp",EDGE,"E7.18.0"),sQuery(id+"F0.wireOp",EDGE,"E7.19.0"),sQuery(id+"F0.wireOp",EDGE,"E7.20.0"),sQuery(id+"F0.wireOp",EDGE,"E7.21.0"),sQuery(id+"F0.wireOp",EDGE,"E7.22.0"),sQuery(id+"F0.wireOp",EDGE,"E7.23.0"),sQuery(id+"F0.wireOp",EDGE,"E7.24.0"),sQuery(id+"F0.wireOp",EDGE,"E7.25.0"),sQuery(id+"F0.wireOp",EDGE,"E7.26.0"),sQuery(id+"F0.wireOp",EDGE,"E7.27.0"),sQuery(id+"F0.wireOp",EDGE,"E7.28.0"),sQuery(id+"F0.wireOp",EDGE,"E7.29.0"),sQuery(id+"F0.wireOp",EDGE,"E8.trimOffspring"),sQuery(id+"F0.wireOp",EDGE,"E9.trimOffspring"),sQuery(id+"F0.wireOp",EDGE,"E10.trimOffspring"),sQuery(id+"F0.wireOp",EDGE,"E11.trimOffspring"),sQuery(id+"F0.wireOp",EDGE,"E12.trimOffspring"),sQuery(id+"F0.wireOp",EDGE,"E13.trimOffspring"),sQuery(id+"F0.wireOp",EDGE,"E14.trimOffspring"),sQuery(id+"F0.wireOp",EDGE,"E15.trimOffspring"),sQuery(id+"F0.wireOp",EDGE,"E16.trimOffspring"),sQuery(id+"F0.wireOp",EDGE,"E17.trimOffspring"),sQuery(id+"F0.wireOp",EDGE,"E18.trimOffspring"),sQuery(id+"F0.wireOp",EDGE,"E19.trimOffspring"),sQuery(id+"F0.wireOp",EDGE,"E20.trimOffspring"),sQuery(id+"F0.wireOp",EDGE,"E21.trimOffspring"),sQuery(id+"F0.wireOp",EDGE,"E22.trimOffspring"),sQuery(id+"F0.wireOp",EDGE,"E23.trimOffspring"),sQuery(id+"F0.wireOp",EDGE,"E24.trimOffspring"),sQuery(id+"F0.wireOp",EDGE,"E25.trimOffspring"),sQuery(id+"F0.wireOp",EDGE,"E26.trimOffspring"),sQuery(id+"F0.wireOp",EDGE,"E27.trimOffspring"),sQuery(id+"F0.wireOp",EDGE,"E28.trimOffspring"),sQuery(id+"F0.wireOp",EDGE,"E29.trimOffspring"),sQuery(id+"F0.wireOp",EDGE,"E30.trimOffspring"),sQuery(id+"F0.wireOp",EDGE,"E31.trimOffspring"),sQuery(id+"F0.wireOp",EDGE,"E32.trimOffspring"),sQuery(id+"F0.wireOp",EDGE,"E33.trimOffspring"),sQuery(id+"F0.wireOp",EDGE,"E34.trimOffspring"),sQuery(id+"F0.wireOp",EDGE,"E35.trimOffspring"),sQuery(id+"F0.wireOp",EDGE,"E36.trimOffspring"),sQuery(id+"F0.wireOp",EDGE,"E47.MirrorCS"),sQuery(id+"F0.wireOp",EDGE,"E45.MirrorCS"),sQuery(id+"F0.wireOp",EDGE,"E40"),sQuery(id+"F0.wireOp",EDGE,"E38"),sQuery(id+"F0.wireOp",EDGE,"E46.MirrorCS"),sQuery(id+"F0.wireOp",EDGE,"E41.filletArc"),sQuery(id+"F0.wireOp",EDGE,"E48.MirrorCS"),sQuery(id+"F0.wireOp",EDGE,"E42.filletArc"),sQuery(id+"F0.wireOp",EDGE,"E39"),sQuery(id+"F0.wireOp",EDGE,"E49.MirrorCS"),sQuery(id+"F0.wireOp",EDGE,"E51.1.38"),sQuery(id+"F0.wireOp",EDGE,"E51.1.39"),sQuery(id+"F0.wireOp",EDGE,"E51.1.40"),sQuery(id+"F0.wireOp",EDGE,"E51.1.42"),sQuery(id+"F0.wireOp",EDGE,"E51.1.46"),sQuery(id+"F0.wireOp",EDGE,"E51.1.47"),sQuery(id+"F0.wireOp",EDGE,"E51.1.56"),sQuery(id+"F0.wireOp",EDGE,"E51.1.62"),sQuery(id+"F0.wireOp",EDGE,"E51.1.68"),sQuery(id+"F0.wireOp",EDGE,"E51.1.69"),sQuery(id+"F0.wireOp",EDGE,"E51.2.38"),sQuery(id+"F0.wireOp",EDGE,"E51.2.39"),sQuery(id+"F0.wireOp",EDGE,"E51.2.40"),sQuery(id+"F0.wireOp",EDGE,"E51.2.42"),sQuery(id+"F0.wireOp",EDGE,"E51.2.46"),sQuery(id+"F0.wireOp",EDGE,"E51.2.47"),sQuery(id+"F0.wireOp",EDGE,"E51.2.56"),sQuery(id+"F0.wireOp",EDGE,"E51.2.62"),sQuery(id+"F0.wireOp",EDGE,"E51.2.68"),sQuery(id+"F0.wireOp",EDGE,"E51.2.69"),sQuery(id+"F0.wireOp",EDGE,"E52.102.3.0"),sQuery(id+"F0.wireOp",EDGE,"E52.106.3.0"),sQuery(id+"F0.wireOp",EDGE,"E52.110.3.0"),sQuery(id+"F0.wireOp",EDGE,"E52.114.3.0"),sQuery(id+"F0.wireOp",EDGE,"E52.121.3.0"),sQuery(id+"F0.wireOp",EDGE,"E52.124.3.0"),sQuery(id+"F0.wireOp",EDGE,"E52.154.3.0"),sQuery(id+"F0.wireOp",EDGE,"E52.178.3.0"),sQuery(id+"F0.wireOp",EDGE,"E52.202.3.0"),sQuery(id+"F0.wireOp",EDGE,"E52.206.3.0"),sQuery(id+"F0.wireOp",EDGE,"E52.102.4.0"),sQuery(id+"F0.wireOp",EDGE,"E52.106.4.0"),sQuery(id+"F0.wireOp",EDGE,"E52.110.4.0"),sQuery(id+"F0.wireOp",EDGE,"E52.114.4.0"),sQuery(id+"F0.wireOp",EDGE,"E52.121.4.0"),sQuery(id+"F0.wireOp",EDGE,"E52.124.4.0"),sQuery(id+"F0.wireOp",EDGE,"E52.154.4.0"),sQuery(id+"F0.wireOp",EDGE,"E52.178.4.0"),sQuery(id+"F0.wireOp",EDGE,"E52.202.4.0"),sQuery(id+"F0.wireOp",EDGE,"E52.206.4.0"),sQuery(id+"F0.wireOp",EDGE,"E53.102.5.0"),sQuery(id+"F0.wireOp",EDGE,"E53.106.5.0"),sQuery(id+"F0.wireOp",EDGE,"E53.110.5.0"),sQuery(id+"F0.wireOp",EDGE,"E53.114.5.0"),sQuery(id+"F0.wireOp",EDGE,"E53.121.5.0"),sQuery(id+"F0.wireOp",EDGE,"E53.124.5.0"),sQuery(id+"F0.wireOp",EDGE,"E53.154.5.0"),sQuery(id+"F0.wireOp",EDGE,"E53.178.5.0"),sQuery(id+"F0.wireOp",EDGE,"E53.202.5.0"),sQuery(id+"F0.wireOp",EDGE,"E53.206.5.0"),sQuery(id+"F0.wireOp",EDGE,"E53.102.6.0"),sQuery(id+"F0.wireOp",EDGE,"E53.106.6.0"),sQuery(id+"F0.wireOp",EDGE,"E53.110.6.0"),sQuery(id+"F0.wireOp",EDGE,"E53.114.6.0"),sQuery(id+"F0.wireOp",EDGE,"E53.121.6.0"),sQuery(id+"F0.wireOp",EDGE,"E53.124.6.0"),sQuery(id+"F0.wireOp",EDGE,"E53.154.6.0"),sQuery(id+"F0.wireOp",EDGE,"E53.178.6.0"),sQuery(id+"F0.wireOp",EDGE,"E53.202.6.0"),sQuery(id+"F0.wireOp",EDGE,"E53.206.6.0"),sQuery(id+"F0.wireOp",EDGE,"E54.102.7.0"),sQuery(id+"F0.wireOp",EDGE,"E54.106.7.0"),sQuery(id+"F0.wireOp",EDGE,"E54.110.7.0"),sQuery(id+"F0.wireOp",EDGE,"E54.114.7.0"),sQuery(id+"F0.wireOp",EDGE,"E54.121.7.0"),sQuery(id+"F0.wireOp",EDGE,"E54.124.7.0"),sQuery(id+"F0.wireOp",EDGE,"E54.154.7.0"),sQuery(id+"F0.wireOp",EDGE,"E54.178.7.0"),sQuery(id+"F0.wireOp",EDGE,"E54.202.7.0"),sQuery(id+"F0.wireOp",EDGE,"E54.206.7.0"),sQuery(id+"F0.wireOp",EDGE,"E54.102.8.0"),sQuery(id+"F0.wireOp",EDGE,"E54.106.8.0"),sQuery(id+"F0.wireOp",EDGE,"E54.110.8.0"),sQuery(id+"F0.wireOp",EDGE,"E54.114.8.0"),sQuery(id+"F0.wireOp",EDGE,"E54.121.8.0"),sQuery(id+"F0.wireOp",EDGE,"E54.124.8.0"),sQuery(id+"F0.wireOp",EDGE,"E54.154.8.0"),sQuery(id+"F0.wireOp",EDGE,"E54.178.8.0"),sQuery(id+"F0.wireOp",EDGE,"E54.202.8.0"),sQuery(id+"F0.wireOp",EDGE,"E54.206.8.0")])],"isStart":false});
            var sketch = newSketch(context, id + "F6", { "sketchPlane" : qUnion([Q0])});
            skCircle(sketch, "E58", {"center": v(0, 17.15) * mm, "radius": 0.76 * mm});
            skCircle(sketch, "E59.1.0.0", {"center": v(0, 15.12) * mm, "radius": 0.76 * mm});
            skCircle(sketch, "E59.2.0.0", {"center": v(0, 13.09) * mm, "radius": 0.76 * mm});
            skLineSegment(sketch, "E59.direction1", {"start": v(0, 17.15) * mm, "end": v(0, 15.12) * mm, "construction": true});
            skLineSegment(sketch, "E60.1.0", {"start": v(-11.02, 13.14) * mm, "end": v(-9.72, 11.58) * mm, "construction": true});
            skCircle(sketch, "E60.1.1", {"center": v(-9.72, 11.58) * mm, "radius": 0.76 * mm});
            skCircle(sketch, "E60.1.2", {"center": v(-11.02, 13.14) * mm, "radius": 0.76 * mm});
            skCircle(sketch, "E60.1.3", {"center": v(-8.41, 10.02) * mm, "radius": 0.76 * mm});
            skLineSegment(sketch, "E60.2.0", {"start": v(-16.89, 2.98) * mm, "end": v(-14.89, 2.63) * mm, "construction": true});
            skCircle(sketch, "E60.2.1", {"center": v(-14.89, 2.63) * mm, "radius": 0.76 * mm});
            skCircle(sketch, "E60.2.2", {"center": v(-16.89, 2.98) * mm, "radius": 0.76 * mm});
            skCircle(sketch, "E60.2.3", {"center": v(-12.89, 2.27) * mm, "radius": 0.76 * mm});
            skLineSegment(sketch, "E60.3.0", {"start": v(-14.85, -8.58) * mm, "end": v(-13.1, -7.56) * mm, "construction": true});
            skCircle(sketch, "E60.3.1", {"center": v(-13.1, -7.56) * mm, "radius": 0.76 * mm});
            skCircle(sketch, "E60.3.2", {"center": v(-14.85, -8.58) * mm, "radius": 0.76 * mm});
            skCircle(sketch, "E60.3.3", {"center": v(-11.33, -6.54) * mm, "radius": 0.76 * mm});
            skLineSegment(sketch, "E60.4.0", {"start": v(-5.87, -16.12) * mm, "end": v(-5.17, -14.2) * mm, "construction": true});
            skCircle(sketch, "E60.4.1", {"center": v(-5.17, -14.2) * mm, "radius": 0.76 * mm});
            skCircle(sketch, "E60.4.2", {"center": v(-5.87, -16.12) * mm, "radius": 0.76 * mm});
            skCircle(sketch, "E60.4.3", {"center": v(-4.48, -12.3) * mm, "radius": 0.76 * mm});
            skLineSegment(sketch, "E60.5.0", {"start": v(5.87, -16.12) * mm, "end": v(5.17, -14.2) * mm, "construction": true});
            skCircle(sketch, "E60.5.1", {"center": v(5.17, -14.2) * mm, "radius": 0.76 * mm});
            skCircle(sketch, "E60.5.2", {"center": v(5.87, -16.12) * mm, "radius": 0.76 * mm});
            skCircle(sketch, "E60.5.3", {"center": v(4.48, -12.3) * mm, "radius": 0.76 * mm});
            skLineSegment(sketch, "E60.6.0", {"start": v(14.85, -8.58) * mm, "end": v(13.1, -7.56) * mm, "construction": true});
            skCircle(sketch, "E60.6.1", {"center": v(13.1, -7.56) * mm, "radius": 0.76 * mm});
            skCircle(sketch, "E60.6.2", {"center": v(14.85, -8.58) * mm, "radius": 0.76 * mm});
            skCircle(sketch, "E60.6.3", {"center": v(11.33, -6.54) * mm, "radius": 0.76 * mm});
            skLineSegment(sketch, "E60.7.0", {"start": v(16.89, 2.98) * mm, "end": v(14.89, 2.63) * mm, "construction": true});
            skCircle(sketch, "E60.7.1", {"center": v(14.89, 2.63) * mm, "radius": 0.76 * mm});
            skCircle(sketch, "E60.7.2", {"center": v(16.89, 2.98) * mm, "radius": 0.76 * mm});
            skCircle(sketch, "E60.7.3", {"center": v(12.89, 2.27) * mm, "radius": 0.76 * mm});
            skLineSegment(sketch, "E60.8.0", {"start": v(11.02, 13.14) * mm, "end": v(9.72, 11.58) * mm, "construction": true});
            skCircle(sketch, "E60.8.1", {"center": v(9.72, 11.58) * mm, "radius": 0.76 * mm});
            skCircle(sketch, "E60.8.2", {"center": v(11.02, 13.14) * mm, "radius": 0.76 * mm});
            skCircle(sketch, "E60.8.3", {"center": v(8.41, 10.02) * mm, "radius": 0.76 * mm});
            skPoint(sketch, "E60.center", {"position": v(0, 0) * mm});
            skCircle(sketch, "E61", {"center": v(0, 31.75) * mm, "radius": 2.22 * mm});
            skSolve(sketch);
        }
        {
            var Q0;
            Q0 = qSketchRegion(id + "F6", true);
            extrude(context, id + "F7", {"entities" : qUnion([Q0]), "operationType" : NewBodyOperationType.REMOVE, "endBound" : BoundingType.THROUGH_ALL, "oppositeDirection" : true, "depth" : 25.4 * mm, "offsetDistance" : 25.4 * mm});
        }
        {
            var Q0;
            Q0=makeQuery(id+"F1.opExtrude","CAP_FACE",FACE,{"disambiguationData":[OSD([sQuery(id+"F0.wireOp",EDGE,"E0"),sQuery(id+"F0.wireOp",EDGE,"E4"),sQuery(id+"F0.wireOp",EDGE,"E7.1.0"),sQuery(id+"F0.wireOp",EDGE,"E7.2.0"),sQuery(id+"F0.wireOp",EDGE,"E7.3.0"),sQuery(id+"F0.wireOp",EDGE,"E7.4.0"),sQuery(id+"F0.wireOp",EDGE,"E7.5.0"),sQuery(id+"F0.wireOp",EDGE,"E7.6.0"),sQuery(id+"F0.wireOp",EDGE,"E7.7.0"),sQuery(id+"F0.wireOp",EDGE,"E7.8.0"),sQuery(id+"F0.wireOp",EDGE,"E7.9.0"),sQuery(id+"F0.wireOp",EDGE,"E7.10.0"),sQuery(id+"F0.wireOp",EDGE,"E7.11.0"),sQuery(id+"F0.wireOp",EDGE,"E7.12.0"),sQuery(id+"F0.wireOp",EDGE,"E7.13.0"),sQuery(id+"F0.wireOp",EDGE,"E7.14.0"),sQuery(id+"F0.wireOp",EDGE,"E7.15.0"),sQuery(id+"F0.wireOp",EDGE,"E7.16.0"),sQuery(id+"F0.wireOp",EDGE,"E7.17.0"),sQuery(id+"F0.wireOp",EDGE,"E7.18.0"),sQuery(id+"F0.wireOp",EDGE,"E7.19.0"),sQuery(id+"F0.wireOp",EDGE,"E7.20.0"),sQuery(id+"F0.wireOp",EDGE,"E7.21.0"),sQuery(id+"F0.wireOp",EDGE,"E7.22.0"),sQuery(id+"F0.wireOp",EDGE,"E7.23.0"),sQuery(id+"F0.wireOp",EDGE,"E7.24.0"),sQuery(id+"F0.wireOp",EDGE,"E7.25.0"),sQuery(id+"F0.wireOp",EDGE,"E7.26.0"),sQuery(id+"F0.wireOp",EDGE,"E7.27.0"),sQuery(id+"F0.wireOp",EDGE,"E7.28.0"),sQuery(id+"F0.wireOp",EDGE,"E7.29.0"),sQuery(id+"F0.wireOp",EDGE,"E8.trimOffspring"),sQuery(id+"F0.wireOp",EDGE,"E9.trimOffspring"),sQuery(id+"F0.wireOp",EDGE,"E10.trimOffspring"),sQuery(id+"F0.wireOp",EDGE,"E11.trimOffspring"),sQuery(id+"F0.wireOp",EDGE,"E12.trimOffspring"),sQuery(id+"F0.wireOp",EDGE,"E13.trimOffspring"),sQuery(id+"F0.wireOp",EDGE,"E14.trimOffspring"),sQuery(id+"F0.wireOp",EDGE,"E15.trimOffspring"),sQuery(id+"F0.wireOp",EDGE,"E16.trimOffspring"),sQuery(id+"F0.wireOp",EDGE,"E17.trimOffspring"),sQuery(id+"F0.wireOp",EDGE,"E18.trimOffspring"),sQuery(id+"F0.wireOp",EDGE,"E19.trimOffspring"),sQuery(id+"F0.wireOp",EDGE,"E20.trimOffspring"),sQuery(id+"F0.wireOp",EDGE,"E21.trimOffspring"),sQuery(id+"F0.wireOp",EDGE,"E22.trimOffspring"),sQuery(id+"F0.wireOp",EDGE,"E23.trimOffspring"),sQuery(id+"F0.wireOp",EDGE,"E24.trimOffspring"),sQuery(id+"F0.wireOp",EDGE,"E25.trimOffspring"),sQuery(id+"F0.wireOp",EDGE,"E26.trimOffspring"),sQuery(id+"F0.wireOp",EDGE,"E27.trimOffspring"),sQuery(id+"F0.wireOp",EDGE,"E28.trimOffspring"),sQuery(id+"F0.wireOp",EDGE,"E29.trimOffspring"),sQuery(id+"F0.wireOp",EDGE,"E30.trimOffspring"),sQuery(id+"F0.wireOp",EDGE,"E31.trimOffspring"),sQuery(id+"F0.wireOp",EDGE,"E32.trimOffspring"),sQuery(id+"F0.wireOp",EDGE,"E33.trimOffspring"),sQuery(id+"F0.wireOp",EDGE,"E34.trimOffspring"),sQuery(id+"F0.wireOp",EDGE,"E35.trimOffspring"),sQuery(id+"F0.wireOp",EDGE,"E36.trimOffspring"),sQuery(id+"F0.wireOp",EDGE,"E47.MirrorCS"),sQuery(id+"F0.wireOp",EDGE,"E45.MirrorCS"),sQuery(id+"F0.wireOp",EDGE,"E40"),sQuery(id+"F0.wireOp",EDGE,"E38"),sQuery(id+"F0.wireOp",EDGE,"E46.MirrorCS"),sQuery(id+"F0.wireOp",EDGE,"E41.filletArc"),sQuery(id+"F0.wireOp",EDGE,"E48.MirrorCS"),sQuery(id+"F0.wireOp",EDGE,"E42.filletArc"),sQuery(id+"F0.wireOp",EDGE,"E39"),sQuery(id+"F0.wireOp",EDGE,"E49.MirrorCS"),sQuery(id+"F0.wireOp",EDGE,"E51.1.38"),sQuery(id+"F0.wireOp",EDGE,"E51.1.39"),sQuery(id+"F0.wireOp",EDGE,"E51.1.40"),sQuery(id+"F0.wireOp",EDGE,"E51.1.42"),sQuery(id+"F0.wireOp",EDGE,"E51.1.46"),sQuery(id+"F0.wireOp",EDGE,"E51.1.47"),sQuery(id+"F0.wireOp",EDGE,"E51.1.56"),sQuery(id+"F0.wireOp",EDGE,"E51.1.62"),sQuery(id+"F0.wireOp",EDGE,"E51.1.68"),sQuery(id+"F0.wireOp",EDGE,"E51.1.69"),sQuery(id+"F0.wireOp",EDGE,"E51.2.38"),sQuery(id+"F0.wireOp",EDGE,"E51.2.39"),sQuery(id+"F0.wireOp",EDGE,"E51.2.40"),sQuery(id+"F0.wireOp",EDGE,"E51.2.42"),sQuery(id+"F0.wireOp",EDGE,"E51.2.46"),sQuery(id+"F0.wireOp",EDGE,"E51.2.47"),sQuery(id+"F0.wireOp",EDGE,"E51.2.56"),sQuery(id+"F0.wireOp",EDGE,"E51.2.62"),sQuery(id+"F0.wireOp",EDGE,"E51.2.68"),sQuery(id+"F0.wireOp",EDGE,"E51.2.69"),sQuery(id+"F0.wireOp",EDGE,"E52.102.3.0"),sQuery(id+"F0.wireOp",EDGE,"E52.106.3.0"),sQuery(id+"F0.wireOp",EDGE,"E52.110.3.0"),sQuery(id+"F0.wireOp",EDGE,"E52.114.3.0"),sQuery(id+"F0.wireOp",EDGE,"E52.121.3.0"),sQuery(id+"F0.wireOp",EDGE,"E52.124.3.0"),sQuery(id+"F0.wireOp",EDGE,"E52.154.3.0"),sQuery(id+"F0.wireOp",EDGE,"E52.178.3.0"),sQuery(id+"F0.wireOp",EDGE,"E52.202.3.0"),sQuery(id+"F0.wireOp",EDGE,"E52.206.3.0"),sQuery(id+"F0.wireOp",EDGE,"E52.102.4.0"),sQuery(id+"F0.wireOp",EDGE,"E52.106.4.0"),sQuery(id+"F0.wireOp",EDGE,"E52.110.4.0"),sQuery(id+"F0.wireOp",EDGE,"E52.114.4.0"),sQuery(id+"F0.wireOp",EDGE,"E52.121.4.0"),sQuery(id+"F0.wireOp",EDGE,"E52.124.4.0"),sQuery(id+"F0.wireOp",EDGE,"E52.154.4.0"),sQuery(id+"F0.wireOp",EDGE,"E52.178.4.0"),sQuery(id+"F0.wireOp",EDGE,"E52.202.4.0"),sQuery(id+"F0.wireOp",EDGE,"E52.206.4.0"),sQuery(id+"F0.wireOp",EDGE,"E53.102.5.0"),sQuery(id+"F0.wireOp",EDGE,"E53.106.5.0"),sQuery(id+"F0.wireOp",EDGE,"E53.110.5.0"),sQuery(id+"F0.wireOp",EDGE,"E53.114.5.0"),sQuery(id+"F0.wireOp",EDGE,"E53.121.5.0"),sQuery(id+"F0.wireOp",EDGE,"E53.124.5.0"),sQuery(id+"F0.wireOp",EDGE,"E53.154.5.0"),sQuery(id+"F0.wireOp",EDGE,"E53.178.5.0"),sQuery(id+"F0.wireOp",EDGE,"E53.202.5.0"),sQuery(id+"F0.wireOp",EDGE,"E53.206.5.0"),sQuery(id+"F0.wireOp",EDGE,"E53.102.6.0"),sQuery(id+"F0.wireOp",EDGE,"E53.106.6.0"),sQuery(id+"F0.wireOp",EDGE,"E53.110.6.0"),sQuery(id+"F0.wireOp",EDGE,"E53.114.6.0"),sQuery(id+"F0.wireOp",EDGE,"E53.121.6.0"),sQuery(id+"F0.wireOp",EDGE,"E53.124.6.0"),sQuery(id+"F0.wireOp",EDGE,"E53.154.6.0"),sQuery(id+"F0.wireOp",EDGE,"E53.178.6.0"),sQuery(id+"F0.wireOp",EDGE,"E53.202.6.0"),sQuery(id+"F0.wireOp",EDGE,"E53.206.6.0"),sQuery(id+"F0.wireOp",EDGE,"E54.102.7.0"),sQuery(id+"F0.wireOp",EDGE,"E54.106.7.0"),sQuery(id+"F0.wireOp",EDGE,"E54.110.7.0"),sQuery(id+"F0.wireOp",EDGE,"E54.114.7.0"),sQuery(id+"F0.wireOp",EDGE,"E54.121.7.0"),sQuery(id+"F0.wireOp",EDGE,"E54.124.7.0"),sQuery(id+"F0.wireOp",EDGE,"E54.154.7.0"),sQuery(id+"F0.wireOp",EDGE,"E54.178.7.0"),sQuery(id+"F0.wireOp",EDGE,"E54.202.7.0"),sQuery(id+"F0.wireOp",EDGE,"E54.206.7.0"),sQuery(id+"F0.wireOp",EDGE,"E54.102.8.0"),sQuery(id+"F0.wireOp",EDGE,"E54.106.8.0"),sQuery(id+"F0.wireOp",EDGE,"E54.110.8.0"),sQuery(id+"F0.wireOp",EDGE,"E54.114.8.0"),sQuery(id+"F0.wireOp",EDGE,"E54.121.8.0"),sQuery(id+"F0.wireOp",EDGE,"E54.124.8.0"),sQuery(id+"F0.wireOp",EDGE,"E54.154.8.0"),sQuery(id+"F0.wireOp",EDGE,"E54.178.8.0"),sQuery(id+"F0.wireOp",EDGE,"E54.202.8.0"),sQuery(id+"F0.wireOp",EDGE,"E54.206.8.0")])],"isStart":false});
            var sketch = newSketch(context, id + "F8", { "sketchPlane" : qUnion([Q0])});
            skCircle(sketch, "E62", {"center": v(2.99, 28.42) * mm, "radius": 1.27 * mm});
            skPoint(sketch, "E63.center", {"position": v(0, 0) * mm});
            skCircle(sketch, "E64.1.0", {"center": v(-2.99, 28.42) * mm, "radius": 1.27 * mm});
            skCircle(sketch, "E64.2.0", {"center": v(-8.83, 27.18) * mm, "radius": 1.27 * mm});
            skCircle(sketch, "E64.3.0", {"center": v(-14.29, 24.75) * mm, "radius": 1.27 * mm});
            skCircle(sketch, "E64.4.0", {"center": v(-19.12, 21.24) * mm, "radius": 1.27 * mm});
            skCircle(sketch, "E64.5.0", {"center": v(-23.12, 16.8) * mm, "radius": 1.27 * mm});
            skCircle(sketch, "E64.6.0", {"center": v(-26.1, 11.62) * mm, "radius": 1.27 * mm});
            skCircle(sketch, "E64.7.0", {"center": v(-27.95, 5.94) * mm, "radius": 1.27 * mm});
            skCircle(sketch, "E64.8.0", {"center": v(-28.57, 0) * mm, "radius": 1.27 * mm});
            skCircle(sketch, "E64.9.0", {"center": v(-27.95, -5.94) * mm, "radius": 1.27 * mm});
            skCircle(sketch, "E64.10.0", {"center": v(-26.1, -11.62) * mm, "radius": 1.27 * mm});
            skCircle(sketch, "E64.11.0", {"center": v(-23.12, -16.8) * mm, "radius": 1.27 * mm});
            skCircle(sketch, "E64.12.0", {"center": v(-19.12, -21.24) * mm, "radius": 1.27 * mm});
            skCircle(sketch, "E64.13.0", {"center": v(-14.29, -24.75) * mm, "radius": 1.27 * mm});
            skCircle(sketch, "E64.14.0", {"center": v(-8.83, -27.18) * mm, "radius": 1.27 * mm});
            skCircle(sketch, "E64.15.0", {"center": v(-2.99, -28.42) * mm, "radius": 1.27 * mm});
            skCircle(sketch, "E64.16.0", {"center": v(2.99, -28.42) * mm, "radius": 1.27 * mm});
            skCircle(sketch, "E64.17.0", {"center": v(8.83, -27.18) * mm, "radius": 1.27 * mm});
            skCircle(sketch, "E64.18.0", {"center": v(14.29, -24.75) * mm, "radius": 1.27 * mm});
            skCircle(sketch, "E64.19.0", {"center": v(19.12, -21.24) * mm, "radius": 1.27 * mm});
            skCircle(sketch, "E64.20.0", {"center": v(23.12, -16.8) * mm, "radius": 1.27 * mm});
            skCircle(sketch, "E64.21.0", {"center": v(26.1, -11.62) * mm, "radius": 1.27 * mm});
            skCircle(sketch, "E64.22.0", {"center": v(27.95, -5.94) * mm, "radius": 1.27 * mm});
            skCircle(sketch, "E64.23.0", {"center": v(28.57, 0) * mm, "radius": 1.27 * mm});
            skCircle(sketch, "E64.24.0", {"center": v(27.95, 5.94) * mm, "radius": 1.27 * mm});
            skCircle(sketch, "E64.25.0", {"center": v(26.1, 11.62) * mm, "radius": 1.27 * mm});
            skCircle(sketch, "E64.26.0", {"center": v(23.12, 16.8) * mm, "radius": 1.27 * mm});
            skCircle(sketch, "E64.27.0", {"center": v(19.12, 21.24) * mm, "radius": 1.27 * mm});
            skCircle(sketch, "E64.28.0", {"center": v(14.29, 24.75) * mm, "radius": 1.27 * mm});
            skCircle(sketch, "E64.29.0", {"center": v(8.83, 27.18) * mm, "radius": 1.27 * mm});
            skSolve(sketch);
        }
        {
            var Q0;
            Q0 = qSketchRegion(id + "F8", true);
            extrude(context, id + "F9", {"entities" : qUnion([Q0]), "operationType" : NewBodyOperationType.REMOVE, "endBound" : BoundingType.THROUGH_ALL, "oppositeDirection" : true, "depth" : 25.4 * mm, "offsetDistance" : 25.4 * mm});
        }
    });
